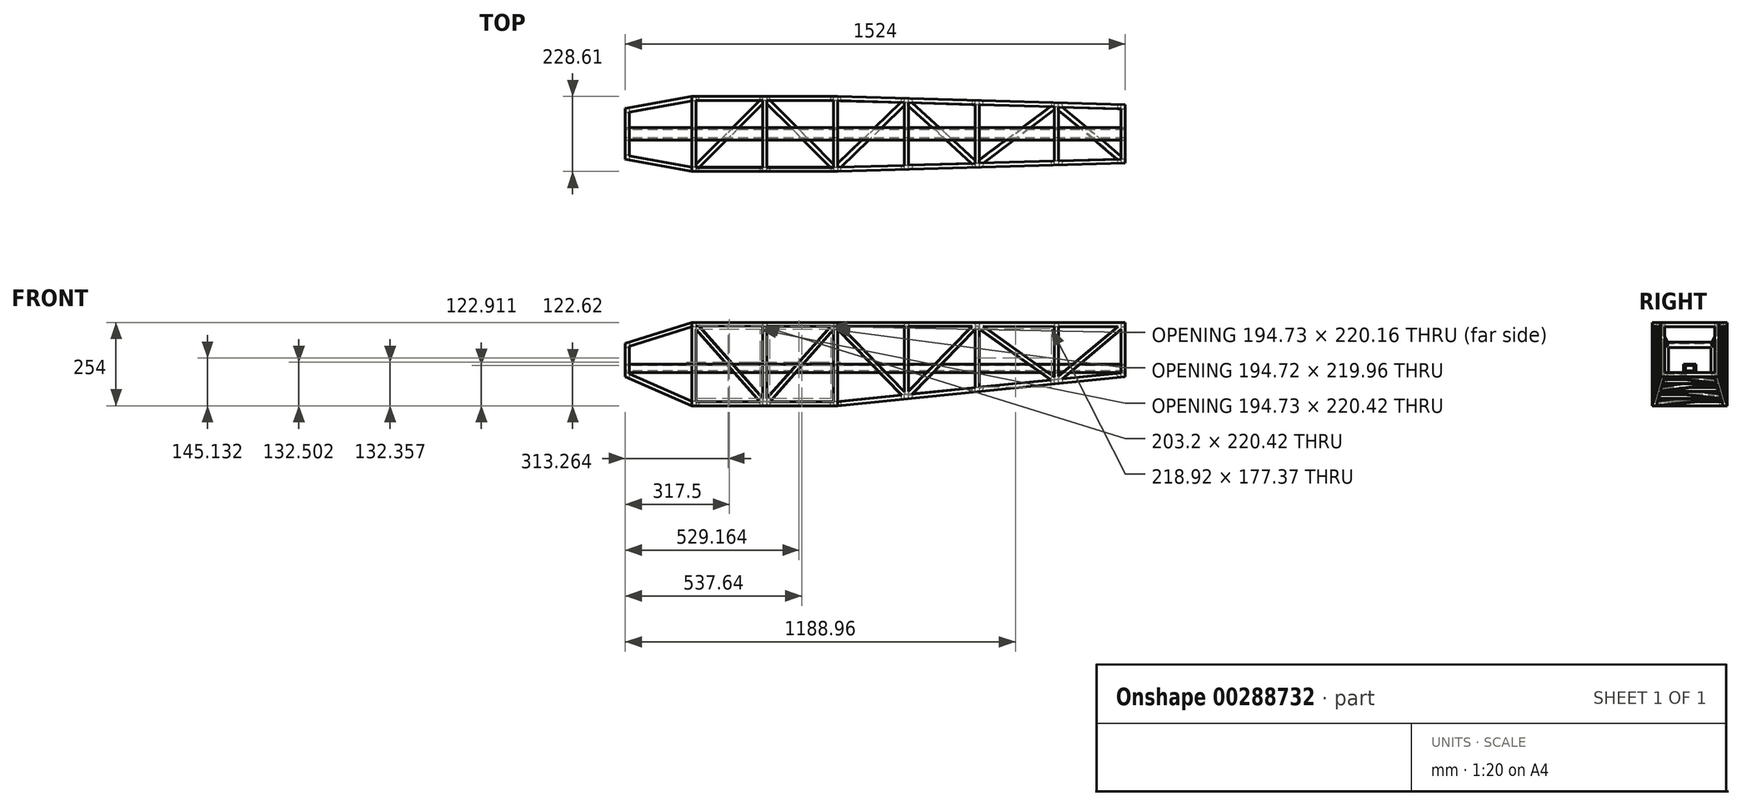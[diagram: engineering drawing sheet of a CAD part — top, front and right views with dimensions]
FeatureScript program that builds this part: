
annotation { "Feature Type Name" : "Feature", "Feature Type Description" : "" }
export const myFeature = defineFeature(function(context is Context, id is Id, definition is map)
    precondition{}
    {
        {
            var Q0;
            Q0=qCreatedBy(makeId("Top.planeOp"),FACE);
            var sketch = newSketch(context, id + "F0", { "sketchPlane" : qUnion([Q0])});
            skLineSegment(sketch, "E0.bottom", {"start": v(762, 177.8) * mm, "end": v(-762, 177.8) * mm});
            skLineSegment(sketch, "E0.top", {"start": v(762, -177.8) * mm, "end": v(-762, -177.8) * mm});
            skLineSegment(sketch, "E0.left", {"start": v(762, 177.8) * mm, "end": v(762, -177.8) * mm});
            skLineSegment(sketch, "E0.right", {"start": v(-762, 177.8) * mm, "end": v(-762, -177.8) * mm});
            skPoint(sketch, "E0.middle", {"position": v(0, 0) * mm});
            skSolve(sketch);
        }
        {
            var Q0;
            Q0=makeQuery(id+"F0.imprint","IMPRINT",FACE,{"disambiguationData":[TD([[makeQuery(id+"F0.imprint","IMPRINT",EDGE,{"derivedFrom":sQuery(id+"F0.wireOp",EDGE,"E0.bottom")}),1.0]])]});
            extrude(context, id + "F1", {"entities" : qUnion([Q0]), "endBound" : BoundingType.SYMMETRIC, "depth" : 254 * mm});
        }
        {
            var Q0;
            Q0=makeQuery(id+"F1.opExtrude","SWEPT_FACE",FACE,{"disambiguationData":[OSD([sQuery(id+"F0.wireOp",EDGE,"E0.left")])]});
            var sketch = newSketch(context, id + "F2", { "sketchPlane" : qUnion([Q0])});
            skLineSegment(sketch, "E1.0", {"start": v(-165.1, -114.3) * mm, "end": v(165.1, -114.3) * mm});
            skLineSegment(sketch, "E1.1", {"start": v(-165.1, 114.3) * mm, "end": v(-165.1, -114.3) * mm});
            skLineSegment(sketch, "E1.2", {"start": v(165.1, 114.3) * mm, "end": v(-165.1, 114.3) * mm});
            skLineSegment(sketch, "E1.3", {"start": v(165.1, -114.3) * mm, "end": v(165.1, 114.3) * mm});
            skSolve(sketch);
        }
        {
            var Q0;
            Q0=makeQuery(id+"F1.opExtrude","CAP_FACE",FACE,{"disambiguationData":[OSD([sQuery(id+"F0.wireOp",EDGE,"E0.bottom"),sQuery(id+"F0.wireOp",EDGE,"E0.top"),sQuery(id+"F0.wireOp",EDGE,"E0.left"),sQuery(id+"F0.wireOp",EDGE,"E0.right")])],"isStart":false});
            var sketch = newSketch(context, id + "F3", { "sketchPlane" : qUnion([Q0])});
            skLineSegment(sketch, "E2.0", {"start": v(-749.3, -165.1) * mm, "end": v(749.3, -165.1) * mm});
            skLineSegment(sketch, "E2.1", {"start": v(-749.3, 165.1) * mm, "end": v(-749.3, -165.1) * mm});
            skLineSegment(sketch, "E2.2", {"start": v(749.3, 165.1) * mm, "end": v(-749.3, 165.1) * mm});
            skLineSegment(sketch, "E2.3", {"start": v(749.3, -165.1) * mm, "end": v(749.3, 165.1) * mm});
            skSolve(sketch);
        }
        {
            var Q0;
            Q0=qCreatedBy(makeId("Front.planeOp"),FACE);
            var sketch = newSketch(context, id + "F4", { "sketchPlane" : qUnion([Q0])});
            skLineSegment(sketch, "E3.0", {"start": v(-762, 127) * mm, "end": v(-762, -127) * mm, "construction": true});
            skLineSegment(sketch, "E4.bottom", {"start": v(-558.8, -143.07) * mm, "end": v(-546.1, -143.07) * mm});
            skLineSegment(sketch, "E4.top", {"start": v(-558.8, 152.62) * mm, "end": v(-546.1, 152.62) * mm});
            skLineSegment(sketch, "E4.left", {"start": v(-558.8, -143.07) * mm, "end": v(-558.8, 152.62) * mm});
            skLineSegment(sketch, "E4.right", {"start": v(-546.1, -143.07) * mm, "end": v(-546.1, 152.62) * mm});
            skLineSegment(sketch, "E5.bottom", {"start": v(-342.9, -143.07) * mm, "end": v(-330.2, -143.07) * mm});
            skLineSegment(sketch, "E5.top", {"start": v(-342.9, 152.62) * mm, "end": v(-330.2, 152.62) * mm});
            skLineSegment(sketch, "E5.left", {"start": v(-342.9, -143.07) * mm, "end": v(-342.9, 152.62) * mm});
            skLineSegment(sketch, "E5.right", {"start": v(-330.2, -143.07) * mm, "end": v(-330.2, 152.62) * mm});
            skLineSegment(sketch, "E6.bottom", {"start": v(-127, -143.07) * mm, "end": v(-114.3, -143.07) * mm});
            skLineSegment(sketch, "E6.top", {"start": v(-127, 152.62) * mm, "end": v(-114.3, 152.62) * mm});
            skLineSegment(sketch, "E6.left", {"start": v(-127, -143.07) * mm, "end": v(-127, 152.62) * mm});
            skLineSegment(sketch, "E6.right", {"start": v(-114.3, -143.07) * mm, "end": v(-114.3, 152.62) * mm});
            skLineSegment(sketch, "E7.bottom", {"start": v(88.9, -143.07) * mm, "end": v(101.6, -143.07) * mm});
            skLineSegment(sketch, "E7.top", {"start": v(88.9, 152.62) * mm, "end": v(101.6, 152.62) * mm});
            skLineSegment(sketch, "E7.left", {"start": v(88.9, -143.07) * mm, "end": v(88.9, 152.62) * mm});
            skLineSegment(sketch, "E7.right", {"start": v(101.6, -143.07) * mm, "end": v(101.6, 152.62) * mm});
            skLineSegment(sketch, "E8", {"start": v(1356.57, 152.62) * mm, "end": v(-852.45, 152.62) * mm, "construction": true});
            skLineSegment(sketch, "E9", {"start": v(1396.25, -143.07) * mm, "end": v(-846.12, -143.07) * mm, "construction": true});
            skLineSegment(sketch, "E10.bottom", {"start": v(254, 152.62) * mm, "end": v(266.7, 152.62) * mm});
            skLineSegment(sketch, "E10.top", {"start": v(254, -143.07) * mm, "end": v(266.7, -143.07) * mm});
            skLineSegment(sketch, "E11.bottom", {"start": v(546.1, -143.07) * mm, "end": v(558.8, -143.07) * mm});
            skLineSegment(sketch, "E11.top", {"start": v(546.1, 152.62) * mm, "end": v(558.8, 152.62) * mm});
            skLineSegment(sketch, "E11.left", {"start": v(546.1, -143.07) * mm, "end": v(546.1, 152.62) * mm});
            skLineSegment(sketch, "E11.right", {"start": v(558.8, -143.07) * mm, "end": v(558.8, 152.62) * mm});
            skLineSegment(sketch, "E12.bottom", {"start": v(304.8, 152.62) * mm, "end": v(317.5, 152.62) * mm});
            skLineSegment(sketch, "E12.top", {"start": v(304.8, -143.07) * mm, "end": v(317.5, -143.07) * mm});
            skLineSegment(sketch, "E12.left", {"start": v(304.8, 152.62) * mm, "end": v(304.8, -143.07) * mm});
            skLineSegment(sketch, "E12.right", {"start": v(317.5, 152.62) * mm, "end": v(317.5, -143.07) * mm});
            skSolve(sketch);
        }
        {
            var Q0;
            Q0=qSketchRegion(id+"F4",true);
            extrude(context, id + "F5", {"entities" : qUnion([Q0]), "operationType" : NewBodyOperationType.ADD, "endBound" : BoundingType.SYMMETRIC, "depth" : 355.6 * mm});
        }
        {
            var Q0;
            Q0=qCreatedBy(makeId("Front.planeOp"),FACE);
            var sketch = newSketch(context, id + "F6", { "sketchPlane" : qUnion([Q0])});
            skLineSegment(sketch, "E13", {"start": v(-822.55, 43.96) * mm, "end": v(-558.8, 127) * mm});
            skLineSegment(sketch, "E14", {"start": v(-558.8, 127) * mm, "end": v(-1015.01, 307.35) * mm});
            skLineSegment(sketch, "E15", {"start": v(-1015.01, 307.35) * mm, "end": v(-822.55, 43.96) * mm});
            skLineSegment(sketch, "E16.0", {"start": v(-762, 127) * mm, "end": v(-762, -127) * mm, "construction": true});
            skLineSegment(sketch, "E17.0", {"start": v(762, 127) * mm, "end": v(762, -127) * mm, "construction": true});
            skLineSegment(sketch, "E18", {"start": v(-762, -38.1) * mm, "end": v(-558.8, -127) * mm});
            skLineSegment(sketch, "E19", {"start": v(-114.3, -127) * mm, "end": v(762, -38.1) * mm});
            skLineSegment(sketch, "E20", {"start": v(-762, -38.1) * mm, "end": v(-810.44, -38.1) * mm});
            skLineSegment(sketch, "E21", {"start": v(-810.44, -38.1) * mm, "end": v(-810.44, -218.05) * mm});
            skLineSegment(sketch, "E22", {"start": v(-810.44, -218.05) * mm, "end": v(819.71, -218.05) * mm});
            skLineSegment(sketch, "E23", {"start": v(819.71, -218.05) * mm, "end": v(819.71, -38.1) * mm});
            skLineSegment(sketch, "E24", {"start": v(819.71, -38.1) * mm, "end": v(762, -38.1) * mm});
            skLineSegment(sketch, "E25", {"start": v(-114.3, -127) * mm, "end": v(-558.8, -127) * mm});
            skSolve(sketch);
        }
        {
            var Q0;
            Q0=makeQuery(id+"F6.imprint","IMPRINT",FACE,{"disambiguationData":[TD([[makeQuery(id+"F6.imprint","IMPRINT",EDGE,{"derivedFrom":sQuery(id+"F6.wireOp",EDGE,"aae6dbfc-d4bc-4c02-a432-3037b792f5ca")}),1.0]])]});
            var Q1;
            Q1=makeQuery(id+"F6.imprint","IMPRINT",FACE,{"disambiguationData":[TD([[makeQuery(id+"F6.imprint","IMPRINT",EDGE,{"derivedFrom":sQuery(id+"F6.wireOp",EDGE,"E13")}),1.0]])]});
            var Q2;
            Q2=makeQuery(id+"F6.imprint","IMPRINT",FACE,{"disambiguationData":[TD([[makeQuery(id+"F6.imprint","IMPRINT",EDGE,{"derivedFrom":sQuery(id+"F6.wireOp",EDGE,"E18")}),-1.0]])]});
            extrude(context, id + "F7", {"entities" : qUnion([Q0, Q1, Q2]), "operationType" : NewBodyOperationType.REMOVE, "endBound" : BoundingType.SYMMETRIC, "oppositeDirection" : true, "depth" : 381 * mm});
        }
        {
            var Q0;
            Q0=qCreatedBy(makeId("Top.planeOp"),FACE);
            var sketch = newSketch(context, id + "F8", { "sketchPlane" : qUnion([Q0])});
            skLineSegment(sketch, "E26", {"start": v(-925.1, 0) * mm, "end": v(877.17, 0) * mm, "construction": true});
            skLineSegment(sketch, "E27", {"start": v(-885.68, 88.9) * mm, "end": v(840.74, 88.9) * mm, "construction": true});
            skLineSegment(sketch, "E28.0", {"start": v(-762, -177.8) * mm, "end": v(-762, 177.8) * mm, "construction": true});
            skLineSegment(sketch, "E29.0", {"start": v(762, 177.8) * mm, "end": v(762, -177.8) * mm, "construction": true});
            skLineSegment(sketch, "E30.0", {"start": v(-342.9, -368.3) * mm, "end": v(-342.9, -88.9) * mm, "construction": true});
            skLineSegment(sketch, "E31.0", {"start": v(101.6, -177.8) * mm, "end": v(101.6, 177.8) * mm, "construction": true});
            skLineSegment(sketch, "E32", {"start": v(762, 0) * mm, "end": v(762, 88.9) * mm});
            skLineSegment(sketch, "E33.0", {"start": v(-114.3, -177.8) * mm, "end": v(-114.3, 177.8) * mm, "construction": true});
            skLineSegment(sketch, "E34", {"start": v(-762, 77.57) * mm, "end": v(-762, 0) * mm});
            skLineSegment(sketch, "E35", {"start": v(-762, 0) * mm, "end": v(-762, 0) * mm});
            skLineSegment(sketch, "E36.MirrorCS", {"start": v(762, 0) * mm, "end": v(762, -88.9) * mm});
            skLineSegment(sketch, "E37.MirrorCS", {"start": v(-762, -77.57) * mm, "end": v(-762, 0) * mm});
            skLineSegment(sketch, "E38.MirrorCS", {"start": v(-885.68, -88.9) * mm, "end": v(840.74, -88.9) * mm, "construction": true});
            skLineSegment(sketch, "E39.MirrorCS", {"start": v(-762, 177.8) * mm, "end": v(-762, -177.8) * mm, "construction": true});
            skLineSegment(sketch, "E40.MirrorCS", {"start": v(762, -177.8) * mm, "end": v(762, 177.8) * mm, "construction": true});
            skLineSegment(sketch, "E41.MirrorCS", {"start": v(-342.9, 368.3) * mm, "end": v(-342.9, 88.9) * mm, "construction": true});
            skLineSegment(sketch, "E42.MirrorCS", {"start": v(-114.3, 177.8) * mm, "end": v(-114.3, -177.8) * mm, "construction": true});
            skLineSegment(sketch, "E43.MirrorCS", {"start": v(101.6, 177.8) * mm, "end": v(101.6, -177.8) * mm, "construction": true});
            skLineSegment(sketch, "E44.bottom", {"start": v(-858.41, 245.19) * mm, "end": v(858.29, 245.19) * mm});
            skLineSegment(sketch, "E44.top", {"start": v(-858.41, -226.45) * mm, "end": v(858.29, -226.45) * mm});
            skLineSegment(sketch, "E44.left", {"start": v(-858.41, 245.19) * mm, "end": v(-858.41, -226.45) * mm});
            skLineSegment(sketch, "E44.right", {"start": v(858.29, 245.19) * mm, "end": v(858.29, -226.45) * mm});
            skLineSegment(sketch, "E45", {"start": v(-342.9, 114.3) * mm, "end": v(-114.3, 114.3) * mm});
            skLineSegment(sketch, "E46.MirrorCS", {"start": v(-342.9, -114.3) * mm, "end": v(-114.3, -114.3) * mm});
            skLineSegment(sketch, "E47", {"start": v(-342.9, 114.3) * mm, "end": v(-558.8, 114.3) * mm});
            skLineSegment(sketch, "E48", {"start": v(-114.3, 114.3) * mm, "end": v(762, 88.9) * mm});
            skLineSegment(sketch, "E49", {"start": v(-342.9, -114.3) * mm, "end": v(-558.8, -114.3) * mm});
            skLineSegment(sketch, "E50", {"start": v(-114.3, -114.3) * mm, "end": v(762, -88.9) * mm});
            skLineSegment(sketch, "E51", {"start": v(-762, 77.57) * mm, "end": v(-558.8, 114.3) * mm});
            skLineSegment(sketch, "E52", {"start": v(-762, -77.57) * mm, "end": v(-558.8, -114.3) * mm});
            skSolve(sketch);
        }
        {
            var Q0;
            Q0=qSketchRegion(id+"F8",true);
            extrude(context, id + "F9", {"entities" : qUnion([Q0]), "operationType" : NewBodyOperationType.REMOVE, "endBound" : BoundingType.SYMMETRIC, "oppositeDirection" : true, "depth" : 381 * mm});
        }
        {
            var Q0;
            Q0=qCreatedBy(makeId("Top.planeOp"),FACE);
            var sketch = newSketch(context, id + "F10", { "sketchPlane" : qUnion([Q0])});
            skLineSegment(sketch, "E53.1", {"start": v(-749.3, -66.96) * mm, "end": v(-749.3, 66.96) * mm});
            skLineSegment(sketch, "E54.1", {"start": v(749.3, 76.56) * mm, "end": v(749.3, -76.56) * mm});
            skLineSegment(sketch, "E55.0", {"start": v(-127, 101.6) * mm, "end": v(-330.2, 101.6) * mm});
            skLineSegment(sketch, "E56.0", {"start": v(-330.2, -101.96) * mm, "end": v(-127, -101.96) * mm});
            skLineSegment(sketch, "E57.0", {"start": v(558.8, 82.08) * mm, "end": v(749.3, 76.56) * mm});
            skLineSegment(sketch, "E58.0", {"start": v(558.8, -82.08) * mm, "end": v(749.3, -76.56) * mm});
            skLineSegment(sketch, "E59.0", {"start": v(-749.3, -66.96) * mm, "end": v(-558.8, -101.4) * mm});
            skLineSegment(sketch, "E60", {"start": v(-342.9, -101.96) * mm, "end": v(-546.1, -101.96) * mm});
            skLineSegment(sketch, "E61", {"start": v(-546.1, 101.6) * mm, "end": v(-342.9, 101.6) * mm});
            skLineSegment(sketch, "E62.0.1", {"start": v(-546.1, -101.96) * mm, "end": v(-546.1, 101.6) * mm});
            skLineSegment(sketch, "E62.0.3", {"start": v(-558.8, 101.4) * mm, "end": v(-558.8, -101.4) * mm});
            skLineSegment(sketch, "E63.0.1", {"start": v(-342.9, 101.6) * mm, "end": v(-342.9, -101.96) * mm});
            skLineSegment(sketch, "E64.0.1", {"start": v(88.9, 95.71) * mm, "end": v(88.9, -95.7) * mm});
            skLineSegment(sketch, "E64.0.3", {"start": v(101.6, -95.34) * mm, "end": v(101.6, 95.34) * mm});
            skLineSegment(sketch, "E65.0.1", {"start": v(304.8, 89.45) * mm, "end": v(304.8, -89.45) * mm});
            skLineSegment(sketch, "E65.0.3", {"start": v(317.5, -89.08) * mm, "end": v(317.5, 89.08) * mm});
            skLineSegment(sketch, "E66.0.1", {"start": v(546.1, 82.45) * mm, "end": v(546.1, -82.45) * mm});
            skLineSegment(sketch, "E66.0.3", {"start": v(558.8, -82.08) * mm, "end": v(558.8, 82.08) * mm});
            skLineSegment(sketch, "E67.trimOffspring", {"start": v(304.8, -89.45) * mm, "end": v(101.6, -95.34) * mm});
            skLineSegment(sketch, "E68.trimOffspring", {"start": v(88.9, -95.7) * mm, "end": v(-114.3, -101.6) * mm});
            skLineSegment(sketch, "E69.trimOffspring", {"start": v(101.6, 95.34) * mm, "end": v(304.8, 89.45) * mm});
            skPoint(sketch, "E62.0.2.end.orphan", {"position": v(-558.8, 114.3) * mm});
            skPoint(sketch, "E62.0.2.start.orphan", {"position": v(-546.1, 114.3) * mm});
            skPoint(sketch, "E70.orphan", {"position": v(-558.8, -114.3) * mm});
            skPoint(sketch, "E71.orphan", {"position": v(-546.1, -114.3) * mm});
            skLineSegment(sketch, "E72", {"start": v(-749.3, 66.96) * mm, "end": v(-558.8, 101.4) * mm});
            skLineSegment(sketch, "E73", {"start": v(-114.3, -101.6) * mm, "end": v(-114.3, 101.6) * mm});
            skLineSegment(sketch, "E74", {"start": v(-330.2, 101.6) * mm, "end": v(-330.2, -101.96) * mm});
            skLineSegment(sketch, "E75", {"start": v(-127, 101.6) * mm, "end": v(-127, -101.96) * mm});
            skLineSegment(sketch, "E76", {"start": v(546.1, -82.45) * mm, "end": v(317.5, -89.08) * mm});
            skLineSegment(sketch, "E77", {"start": v(88.9, 95.71) * mm, "end": v(-114.3, 101.6) * mm});
            skLineSegment(sketch, "E78", {"start": v(546.1, 82.45) * mm, "end": v(317.5, 89.08) * mm});
            skSolve(sketch);
        }
        {
            var Q0;
            Q0=qSketchRegion(id+"F10",true);
            extrude(context, id + "F11", {"entities" : qUnion([Q0]), "operationType" : NewBodyOperationType.REMOVE, "endBound" : BoundingType.SYMMETRIC, "depth" : 381 * mm});
        }
        {
            var Q0;
            Q0=qCreatedBy(makeId("Front.planeOp"),FACE);
            var sketch = newSketch(context, id + "F12", { "sketchPlane" : qUnion([Q0])});
            skLineSegment(sketch, "E79.0", {"start": v(-749.3, 53.7) * mm, "end": v(-558.8, 113.69) * mm});
            skLineSegment(sketch, "E79.1", {"start": v(-749.3, -29.8) * mm, "end": v(-749.3, 53.7) * mm});
            skLineSegment(sketch, "E79.2", {"start": v(-749.3, -29.8) * mm, "end": v(-558.8, -113.14) * mm});
            skLineSegment(sketch, "E79.3", {"start": v(-342.9, -114.3) * mm, "end": v(-546.1, -114.3) * mm});
            skLineSegment(sketch, "E80.0", {"start": v(749.3, -26.62) * mm, "end": v(558.8, -45.95) * mm});
            skLineSegment(sketch, "E80.1", {"start": v(749.3, -26.62) * mm, "end": v(749.3, 114.3) * mm});
            skLineSegment(sketch, "E80.2", {"start": v(558.8, 114.3) * mm, "end": v(749.3, 114.3) * mm});
            skLineSegment(sketch, "E81", {"start": v(-127, -114.36) * mm, "end": v(-330.2, -114.3) * mm});
            skLineSegment(sketch, "E82.0.1", {"start": v(558.8, 114.3) * mm, "end": v(558.8, -45.95) * mm});
            skLineSegment(sketch, "E83.0.1", {"start": v(101.6, 114.89) * mm, "end": v(101.6, -92.46) * mm});
            skLineSegment(sketch, "E83.0.3", {"start": v(304.8, -71.84) * mm, "end": v(304.8, 114.63) * mm});
            skLineSegment(sketch, "E84.0.0", {"start": v(-330.2, 115.44) * mm, "end": v(-330.2, -114.3) * mm});
            skLineSegment(sketch, "E84.0.2", {"start": v(-127, -114.36) * mm, "end": v(-127, 115.18) * mm});
            skLineSegment(sketch, "E85.0.1", {"start": v(-546.1, 115.71) * mm, "end": v(-546.1, -114.3) * mm});
            skLineSegment(sketch, "E85.0.3", {"start": v(-342.9, -114.3) * mm, "end": v(-342.9, 115.45) * mm});
            skLineSegment(sketch, "E86.0.2", {"start": v(-558.8, -113.14) * mm, "end": v(-558.8, 113.69) * mm});
            skPoint(sketch, "E82.0.0.start.orphan", {"position": v(749.3, 127) * mm});
            skPoint(sketch, "E87.orphan", {"position": v(558.8, 127) * mm});
            skPoint(sketch, "E88.0.0.start.orphan", {"position": v(558.8, 126.99) * mm});
            skLineSegment(sketch, "E89.trimOffspring", {"start": v(304.8, 114.63) * mm, "end": v(101.6, 114.89) * mm});
            skPoint(sketch, "E83.0.0.start.orphan", {"position": v(304.8, 127) * mm});
            skLineSegment(sketch, "E90.trimOffspring", {"start": v(-127, 115.18) * mm, "end": v(-330.2, 115.44) * mm});
            skPoint(sketch, "E84.0.1.end.orphan", {"position": v(-127, -127) * mm});
            skPoint(sketch, "E91.orphan", {"position": v(-330.2, -127) * mm});
            skLineSegment(sketch, "E92.trimOffspring", {"start": v(-342.9, 115.45) * mm, "end": v(-546.1, 115.71) * mm});
            skPoint(sketch, "E84.0.3.end.orphan", {"position": v(-330.2, 127) * mm});
            skPoint(sketch, "E84.0.3.start.orphan", {"position": v(-127, 127) * mm});
            skPoint(sketch, "E85.0.2.end.orphan", {"position": v(-342.9, -127) * mm});
            skPoint(sketch, "E93.orphan", {"position": v(-546.1, -127) * mm});
            skPoint(sketch, "E94.orphan", {"position": v(-546.1, 127) * mm});
            skPoint(sketch, "E86.0.3.start.orphan", {"position": v(-558.8, 127) * mm});
            skPoint(sketch, "E95.orphan", {"position": v(101.6, 127) * mm});
            skLineSegment(sketch, "E96", {"start": v(546.1, -48.1) * mm, "end": v(456.3, -56.47) * mm});
            skPoint(sketch, "E82.0.2.end.orphan", {"position": v(749.3, -39.39) * mm});
            skPoint(sketch, "E97.orphan", {"position": v(-342.9, 127) * mm});
            skLineSegment(sketch, "E98.left", {"start": v(-680.76, 244.02) * mm, "end": v(-680.76, 242.67) * mm});
            skLineSegment(sketch, "E98.right", {"start": v(-640.08, 244.02) * mm, "end": v(-640.08, 242.67) * mm});
            skLineSegment(sketch, "E99.bottom", {"start": v(851.63, 270.75) * mm, "end": v(-718.73, 270.75) * mm});
            skLineSegment(sketch, "E99.top", {"start": v(851.63, 127) * mm, "end": v(-718.73, 127) * mm});
            skLineSegment(sketch, "E99.left", {"start": v(851.63, 270.75) * mm, "end": v(851.63, 127) * mm});
            skLineSegment(sketch, "E99.right", {"start": v(-718.73, 270.75) * mm, "end": v(-718.73, 127) * mm});
            skLineSegment(sketch, "E100", {"start": v(-114.3, -114.36) * mm, "end": v(88.9, -93.75) * mm});
            skLineSegment(sketch, "E101", {"start": v(546.1, 114.3) * mm, "end": v(317.5, 114.61) * mm});
            skLineSegment(sketch, "E102", {"start": v(88.9, 114.9) * mm, "end": v(-114.3, 115.18) * mm});
            skLineSegment(sketch, "E103", {"start": v(-114.3, 115.18) * mm, "end": v(-114.3, -114.36) * mm});
            skLineSegment(sketch, "E104", {"start": v(88.9, 114.9) * mm, "end": v(88.9, -93.75) * mm});
            skLineSegment(sketch, "E105", {"start": v(317.5, 114.61) * mm, "end": v(317.5, -70.55) * mm});
            skLineSegment(sketch, "E106", {"start": v(546.1, 114.3) * mm, "end": v(546.1, -48.1) * mm});
            skLineSegment(sketch, "E107.trimOffspring", {"start": v(317.5, -70.55) * mm, "end": v(456.3, -56.47) * mm});
            skLineSegment(sketch, "E108.trimOffspring", {"start": v(101.6, -92.46) * mm, "end": v(304.8, -71.84) * mm});
            skSolve(sketch);
        }
        {
            var Q0;
            Q0=qSketchRegion(id+"F12",true);
            extrude(context, id + "F13", {"entities" : qUnion([Q0]), "operationType" : NewBodyOperationType.REMOVE, "endBound" : BoundingType.SYMMETRIC, "oppositeDirection" : true, "depth" : 381 * mm});
        }
        {
            var Q0;
            {var subQ4=sQuery(id+"F4.wireOp",EDGE,"E4.top");var subQ11=sQuery(id+"F4.wireOp",EDGE,"E4.left");Q0=makeQuery(id+"F13.boolean.opBoolean","MERGE",FACE,{"derivedFrom":[makeQuery(id+"F11.boolean.opBoolean","MERGE",FACE,{"derivedFrom":[makeQuery(id+"F5.boolean.opBoolean","SPLIT",FACE,{"disambiguationData":[TD([makeQuery(id+"F5.opExtrude","SWEPT_FACE",FACE,{"disambiguationData":[OSD([subQ4])]})])],"derivedFrom":makeQuery(id+"F5.opExtrude","SWEPT_FACE",FACE,{"disambiguationData":[OSD([subQ11])]})}),makeQuery(id+"F11.opExtrude","SWEPT_FACE",FACE,{"disambiguationData":[OSD([sQuery(id+"F10.wireOp",EDGE,"76c89935-962c-43c5-8293-adbbc792d1c5.0")])]})]}),makeQuery(id+"F13.opExtrude","SWEPT_FACE",FACE,{"disambiguationData":[OSD([sQuery(id+"F12.wireOp",EDGE,"9ef2c277-a94d-4be6-9fd4-f6ea86bf56da.0.3")])]})]});}
            var sketch = newSketch(context, id + "F14", { "sketchPlane" : qUnion([Q0])});
            skLineSegment(sketch, "E109.bottom", {"start": v(-101.4, 113.69) * mm, "end": v(101.4, 113.69) * mm});
            skLineSegment(sketch, "E109.top", {"start": v(-101.4, -113.14) * mm, "end": v(101.4, -113.14) * mm});
            skLineSegment(sketch, "E109.left", {"start": v(-101.4, 113.69) * mm, "end": v(-101.4, -113.14) * mm});
            skLineSegment(sketch, "E109.right", {"start": v(101.4, 113.69) * mm, "end": v(101.4, -113.14) * mm});
            skSolve(sketch);
        }
        {
            var Q0;
            Q0=qSketchRegion(id+"F14",true);
            extrude(context, id + "F15", {"entities" : qUnion([Q0]), "operationType" : NewBodyOperationType.REMOVE, "oppositeDirection" : true, "depth" : 25.4 * mm});
        }
        {
            var Q0;
            {var subQ1=sQuery(id+"F4.wireOp",EDGE,"E5.left");var subQ2=sQuery(id+"F4.wireOp",EDGE,"E5.top");Q0=makeQuery(id+"F13.boolean.opBoolean","MERGE",FACE,{"derivedFrom":[makeQuery(id+"F11.boolean.opBoolean","MERGE",FACE,{"derivedFrom":[makeQuery(id+"F5.boolean.opBoolean","SPLIT",FACE,{"disambiguationData":[TD([makeQuery(id+"F5.opExtrude","SWEPT_FACE",FACE,{"disambiguationData":[OSD([subQ2])]})])],"derivedFrom":makeQuery(id+"F5.opExtrude","SWEPT_FACE",FACE,{"disambiguationData":[OSD([subQ1])]})}),makeQuery(id+"F11.opExtrude","SWEPT_FACE",FACE,{"disambiguationData":[OSD([sQuery(id+"F10.wireOp",EDGE,"7b3102ac-ed15-4f5d-bc17-57cfcd7eebf1.0")])]})]}),makeQuery(id+"F13.opExtrude","SWEPT_FACE",FACE,{"disambiguationData":[OSD([sQuery(id+"F12.wireOp",EDGE,"8vpACN4d-Oada-hr1t-Xb63-NezVnV2j5PEM")])]})]});}
            var sketch = newSketch(context, id + "F16", { "sketchPlane" : qUnion([Q0])});
            skLineSegment(sketch, "E110.bottom", {"start": v(-101.6, 115.45) * mm, "end": v(101.96, 115.45) * mm});
            skLineSegment(sketch, "E110.top", {"start": v(-101.6, -114.3) * mm, "end": v(101.96, -114.3) * mm});
            skLineSegment(sketch, "E110.left", {"start": v(-101.6, 115.45) * mm, "end": v(-101.6, -114.3) * mm});
            skLineSegment(sketch, "E110.right", {"start": v(101.96, 115.45) * mm, "end": v(101.96, -114.3) * mm});
            skSolve(sketch);
        }
        {
            var Q0;
            Q0=qSketchRegion(id+"F16",true);
            extrude(context, id + "F17", {"entities" : qUnion([Q0]), "operationType" : NewBodyOperationType.REMOVE, "oppositeDirection" : true, "depth" : 25.4 * mm});
        }
        {
            var Q0;
            {var subQ8=sQuery(id+"F4.wireOp",EDGE,"E6.top");var subQ16=sQuery(id+"F4.wireOp",EDGE,"E6.left");Q0=makeQuery(id+"F13.boolean.opBoolean","MERGE",FACE,{"derivedFrom":[makeQuery(id+"F11.boolean.opBoolean","MERGE",FACE,{"derivedFrom":[makeQuery(id+"F5.boolean.opBoolean","SPLIT",FACE,{"disambiguationData":[TD([makeQuery(id+"F5.opExtrude","SWEPT_FACE",FACE,{"disambiguationData":[OSD([subQ8])]})])],"derivedFrom":makeQuery(id+"F5.opExtrude","SWEPT_FACE",FACE,{"disambiguationData":[OSD([subQ16])]})}),makeQuery(id+"F11.opExtrude","SWEPT_FACE",FACE,{"disambiguationData":[OSD([sQuery(id+"F10.wireOp",EDGE,"b35c1112-db7b-4928-a18e-9a17467dcdab.0")])]})]}),makeQuery(id+"F13.opExtrude","SWEPT_FACE",FACE,{"disambiguationData":[OSD([sQuery(id+"F12.wireOp",EDGE,"fa40cc79-636a-4cbc-a25d-f27d8fe22ac2.0.3")])]})]});}
            var sketch = newSketch(context, id + "F18", { "sketchPlane" : qUnion([Q0])});
            skLineSegment(sketch, "E111.bottom", {"start": v(-101.6, 115.18) * mm, "end": v(101.96, 115.18) * mm});
            skLineSegment(sketch, "E111.top", {"start": v(-101.6, -114.36) * mm, "end": v(101.96, -114.36) * mm});
            skLineSegment(sketch, "E111.left", {"start": v(-101.6, 115.18) * mm, "end": v(-101.6, -114.36) * mm});
            skLineSegment(sketch, "E111.right", {"start": v(101.96, 115.18) * mm, "end": v(101.96, -114.36) * mm});
            skSolve(sketch);
        }
        {
            var Q0;
            Q0=qSketchRegion(id+"F18",true);
            extrude(context, id + "F19", {"entities" : qUnion([Q0]), "operationType" : NewBodyOperationType.REMOVE, "oppositeDirection" : true, "depth" : 25.4 * mm});
        }
        {
            var Q0;
            {var subQ0=sQuery(id+"F4.wireOp",EDGE,"E7.bottom");var subQ36=sQuery(id+"F4.wireOp",EDGE,"E7.left");var subQ37=sQuery(id+"F4.wireOp",EDGE,"E7.top");var subQ60=makeQuery(id+"F5.opExtrude","SWEPT_FACE",FACE,{"disambiguationData":[OSD([subQ36])]});Q0=makeQuery(id+"F13.boolean.opBoolean","MERGE",FACE,{"derivedFrom":[makeQuery(id+"F11.boolean.opBoolean","MERGE",FACE,{"derivedFrom":[makeQuery(id+"F5.boolean.opBoolean","SPLIT",FACE,{"disambiguationData":[TD([makeQuery(id+"F5.opExtrude","SWEPT_FACE",FACE,{"disambiguationData":[OSD([subQ37])]})])],"derivedFrom":subQ60}),makeQuery(id+"F5.boolean.opBoolean","SPLIT",FACE,{"disambiguationData":[TD([makeQuery(id+"F5.opExtrude","SWEPT_FACE",FACE,{"disambiguationData":[OSD([subQ0])]})])],"derivedFrom":subQ60}),makeQuery(id+"F11.opExtrude","SWEPT_FACE",FACE,{"disambiguationData":[OSD([sQuery(id+"F10.wireOp",EDGE,"7310f20e-b108-4276-8773-8cf4f74fe12c.0")])]})]}),makeQuery(id+"F13.opExtrude","SWEPT_FACE",FACE,{"disambiguationData":[OSD([sQuery(id+"F12.wireOp",EDGE,"FrRoJ9V7-tiAn-pTb4-UzEj-WxOpO9FH2ecp")])]})]});}
            var sketch = newSketch(context, id + "F20", { "sketchPlane" : qUnion([Q0])});
            skLineSegment(sketch, "E112.bottom", {"start": v(-95.71, 114.9) * mm, "end": v(95.7, 114.9) * mm});
            skLineSegment(sketch, "E112.top", {"start": v(-95.71, -93.75) * mm, "end": v(95.7, -93.75) * mm});
            skLineSegment(sketch, "E112.left", {"start": v(-95.71, 114.9) * mm, "end": v(-95.71, -93.75) * mm});
            skLineSegment(sketch, "E112.right", {"start": v(95.7, 114.9) * mm, "end": v(95.7, -93.75) * mm});
            skSolve(sketch);
        }
        {
            var Q0;
            Q0=qSketchRegion(id+"F20",true);
            extrude(context, id + "F21", {"entities" : qUnion([Q0]), "operationType" : NewBodyOperationType.REMOVE, "oppositeDirection" : true, "depth" : 25.4 * mm});
        }
        {
            var Q0;
            {var subQ35=sQuery(id+"F4.wireOp",EDGE,"E12.left");var subQ37=sQuery(id+"F4.wireOp",EDGE,"E12.bottom");Q0=makeQuery(id+"F13.boolean.opBoolean","MERGE",FACE,{"derivedFrom":[makeQuery(id+"F11.boolean.opBoolean","MERGE",FACE,{"derivedFrom":[makeQuery(id+"F5.boolean.opBoolean","SPLIT",FACE,{"disambiguationData":[TD([makeQuery(id+"F5.opExtrude","SWEPT_FACE",FACE,{"disambiguationData":[OSD([subQ37])]})])],"derivedFrom":makeQuery(id+"F5.opExtrude","SWEPT_FACE",FACE,{"disambiguationData":[OSD([subQ35])]})}),makeQuery(id+"F11.opExtrude","SWEPT_FACE",FACE,{"disambiguationData":[OSD([sQuery(id+"F10.wireOp",EDGE,"b7ba8543-acbf-43cf-88d8-2159336d2e7e.0")])]})]}),makeQuery(id+"F13.opExtrude","SWEPT_FACE",FACE,{"disambiguationData":[OSD([sQuery(id+"F12.wireOp",EDGE,"MzW9eNza-KUkf-pAGu-OPrh-YCygVrhiN9A4")])]})]});}
            var sketch = newSketch(context, id + "F22", { "sketchPlane" : qUnion([Q0])});
            skLineSegment(sketch, "E113.bottom", {"start": v(-89.45, 114.63) * mm, "end": v(89.45, 114.63) * mm});
            skLineSegment(sketch, "E113.top", {"start": v(-89.45, -71.84) * mm, "end": v(89.45, -71.84) * mm});
            skLineSegment(sketch, "E113.left", {"start": v(-89.45, 114.63) * mm, "end": v(-89.45, -71.84) * mm});
            skLineSegment(sketch, "E113.right", {"start": v(89.45, 114.63) * mm, "end": v(89.45, -71.84) * mm});
            skSolve(sketch);
        }
        {
            var Q0;
            Q0=qSketchRegion(id+"F22",true);
            extrude(context, id + "F23", {"entities" : qUnion([Q0]), "operationType" : NewBodyOperationType.REMOVE, "oppositeDirection" : true, "depth" : 15.24 * mm});
        }
        {
            var Q0;
            {var subQ18=sQuery(id+"F4.wireOp",EDGE,"E11.left");var subQ19=sQuery(id+"F4.wireOp",EDGE,"E11.top");Q0=makeQuery(id+"F13.boolean.opBoolean","MERGE",FACE,{"derivedFrom":[makeQuery(id+"F11.boolean.opBoolean","MERGE",FACE,{"derivedFrom":[makeQuery(id+"F5.boolean.opBoolean","SPLIT",FACE,{"disambiguationData":[TD([makeQuery(id+"F5.opExtrude","SWEPT_FACE",FACE,{"disambiguationData":[OSD([subQ19])]})])],"derivedFrom":makeQuery(id+"F5.opExtrude","SWEPT_FACE",FACE,{"disambiguationData":[OSD([subQ18])]})}),makeQuery(id+"F11.opExtrude","SWEPT_FACE",FACE,{"disambiguationData":[OSD([sQuery(id+"F10.wireOp",EDGE,"94f42aec-5a63-4bb3-a17e-c23af455982a.0")])]})]}),makeQuery(id+"F13.opExtrude","SWEPT_FACE",FACE,{"disambiguationData":[OSD([sQuery(id+"F12.wireOp",EDGE,"4bo9Z2lR-88Dg-C45D-lGNA-9ZzvTnCFj7b6")])]})]});}
            var sketch = newSketch(context, id + "F24", { "sketchPlane" : qUnion([Q0])});
            skLineSegment(sketch, "E114.bottom", {"start": v(-82.45, 114.3) * mm, "end": v(82.45, 114.3) * mm});
            skLineSegment(sketch, "E114.top", {"start": v(-82.45, -48.1) * mm, "end": v(82.45, -48.1) * mm});
            skLineSegment(sketch, "E114.left", {"start": v(82.45, 114.3) * mm, "end": v(82.45, -48.1) * mm});
            skLineSegment(sketch, "E114.right", {"start": v(-82.45, 114.3) * mm, "end": v(-82.45, -48.1) * mm});
            skSolve(sketch);
        }
        {
            var Q0;
            Q0=qSketchRegion(id+"F24",true);
            extrude(context, id + "F25", {"entities" : qUnion([Q0]), "operationType" : NewBodyOperationType.REMOVE, "oppositeDirection" : true, "depth" : 13.97 * mm});
        }
        {
            var Q0;
            Q0=makeQuery(id+"F1.opExtrude","SWEPT_FACE",FACE,{"disambiguationData":[OSD([sQuery(id+"F0.wireOp",EDGE,"E0.left")])]});
            var sketch = newSketch(context, id + "F26", { "sketchPlane" : qUnion([Q0])});
            skLineSegment(sketch, "E115.bottom", {"start": v(-76.2, 114.3) * mm, "end": v(76.2, 114.3) * mm});
            skLineSegment(sketch, "E115.top", {"start": v(-76.2, -25.4) * mm, "end": v(76.2, -25.4) * mm});
            skLineSegment(sketch, "E115.left", {"start": v(-76.2, 114.3) * mm, "end": v(-76.2, -25.4) * mm});
            skLineSegment(sketch, "E115.right", {"start": v(76.2, 114.3) * mm, "end": v(76.2, -25.4) * mm});
            skSolve(sketch);
        }
        {
            var Q0;
            Q0=makeQuery(id+"F26.imprint","IMPRINT",FACE,{"disambiguationData":[TD([[makeQuery(id+"F26.imprint","IMPRINT",EDGE,{"derivedFrom":sQuery(id+"F26.wireOp",EDGE,"E115.bottom")}),-1.0]])]});
            extrude(context, id + "F27", {"entities" : qUnion([Q0]), "operationType" : NewBodyOperationType.REMOVE, "oppositeDirection" : true, "depth" : 12.7 * mm});
        }
        {
            var Q0;
            Q0=makeQuery(id+"F9.boolean.opBoolean","COPY",FACE,{"derivedFrom":makeQuery(id+"F9.opExtrude","SWEPT_FACE",FACE,{"disambiguationData":[OSD([sQuery(id+"F8.wireOp",EDGE,"E50")])]})});
            var sketch = newSketch(context, id + "F28", { "sketchPlane" : qUnion([Q0])});
            skLineSegment(sketch, "E116", {"start": v(746.4, 114.3) * mm, "end": v(555.82, -45.95) * mm, "construction": true});
            skLineSegment(sketch, "E117", {"start": v(543.11, -48.1) * mm, "end": v(314.42, 114.61) * mm, "construction": true});
            skLineSegment(sketch, "E118", {"start": v(301.71, 114.63) * mm, "end": v(98.43, -92.46) * mm, "construction": true});
            skLineSegment(sketch, "E119", {"start": v(85.72, -93.75) * mm, "end": v(-117.56, 115.18) * mm, "construction": true});
            skLineSegment(sketch, "E120", {"start": v(746.4, 106) * mm, "end": v(567.04, -44.81) * mm});
            skLineSegment(sketch, "E121", {"start": v(533.43, -49) * mm, "end": v(314.42, 106.82) * mm});
            skLineSegment(sketch, "E122", {"start": v(108.3, -91.45) * mm, "end": v(301.71, 105.56) * mm});
            skLineSegment(sketch, "E123", {"start": v(-117.56, 106.07) * mm, "end": v(77.66, -94.56) * mm});
            skLineSegment(sketch, "E124.MirrorCS", {"start": v(736.53, 114.3) * mm, "end": v(558.87, -35.1) * mm});
            skLineSegment(sketch, "E125.MirrorCS", {"start": v(540.8, -38.66) * mm, "end": v(325.4, 114.6) * mm});
            skLineSegment(sketch, "E126.MirrorCS", {"start": v(99.25, -82.56) * mm, "end": v(292.65, 114.46) * mm});
            skLineSegment(sketch, "E127.MirrorCS", {"start": v(-108.46, 114.93) * mm, "end": v(85.72, -84.64) * mm});
            skPoint(sketch, "E128", {"position": v(736.53, 114.3) * mm});
            skPoint(sketch, "E129", {"position": v(325.4, 114.6) * mm});
            skPoint(sketch, "E130", {"position": v(85.72, -84.64) * mm});
            skPoint(sketch, "E131.orphan", {"position": v(738.23, 115.72) * mm});
            skLineSegment(sketch, "E132", {"start": v(558.87, -35.1) * mm, "end": v(555.82, -37.65) * mm});
            skLineSegment(sketch, "E133", {"start": v(540.8, -38.66) * mm, "end": v(543.11, -40.3) * mm});
            skPoint(sketch, "E134.orphan", {"position": v(321.78, 117.17) * mm});
            skLineSegment(sketch, "E135", {"start": v(292.65, 114.46) * mm, "end": v(292.83, 114.64) * mm});
            skLineSegment(sketch, "E136", {"start": v(99.25, -82.56) * mm, "end": v(98.43, -83.4) * mm});
            skPoint(sketch, "E137.orphan", {"position": v(86.76, -85.7) * mm});
            skLineSegment(sketch, "E138", {"start": v(-108.46, 114.93) * mm, "end": v(-108.7, 115.17) * mm});
            skLineSegment(sketch, "E139", {"start": v(-108.7, 115.17) * mm, "end": v(-117.56, 115.18) * mm});
            skLineSegment(sketch, "E140", {"start": v(-117.56, 115.18) * mm, "end": v(-117.56, 106.07) * mm});
            skLineSegment(sketch, "E141", {"start": v(85.72, -84.64) * mm, "end": v(85.72, -93.75) * mm});
            skLineSegment(sketch, "E142", {"start": v(77.66, -94.56) * mm, "end": v(85.72, -93.75) * mm});
            skLineSegment(sketch, "E143", {"start": v(98.43, -83.4) * mm, "end": v(98.43, -92.46) * mm});
            skLineSegment(sketch, "E144", {"start": v(108.3, -91.45) * mm, "end": v(98.43, -92.46) * mm});
            skLineSegment(sketch, "E145", {"start": v(301.71, 105.56) * mm, "end": v(301.71, 114.63) * mm});
            skLineSegment(sketch, "E146", {"start": v(292.83, 114.64) * mm, "end": v(301.71, 114.63) * mm});
            skLineSegment(sketch, "E147", {"start": v(325.4, 114.6) * mm, "end": v(314.42, 114.61) * mm});
            skLineSegment(sketch, "E148", {"start": v(314.42, 106.82) * mm, "end": v(314.42, 114.61) * mm});
            skLineSegment(sketch, "E149", {"start": v(533.43, -49) * mm, "end": v(543.11, -48.1) * mm});
            skLineSegment(sketch, "E150", {"start": v(543.11, -40.3) * mm, "end": v(543.11, -48.1) * mm});
            skLineSegment(sketch, "E151", {"start": v(555.82, -37.65) * mm, "end": v(555.82, -45.95) * mm});
            skLineSegment(sketch, "E152", {"start": v(567.04, -44.81) * mm, "end": v(555.82, -45.95) * mm});
            skLineSegment(sketch, "E153", {"start": v(746.4, 106) * mm, "end": v(746.4, 114.3) * mm});
            skLineSegment(sketch, "E154", {"start": v(736.53, 114.3) * mm, "end": v(746.4, 114.3) * mm});
            skSolve(sketch);
        }
        {
            var Q0;
            Q0=makeQuery(id+"F9.boolean.opBoolean","COPY",FACE,{"derivedFrom":makeQuery(id+"F9.opExtrude","SWEPT_FACE",FACE,{"disambiguationData":[OSD([sQuery(id+"F8.wireOp",EDGE,"E46.MirrorCS")])]})});
            var sketch = newSketch(context, id + "F29", { "sketchPlane" : qUnion([Q0])});
            skLineSegment(sketch, "E155", {"start": v(-127, 115.18) * mm, "end": v(-330.2, -114.3) * mm, "construction": true});
            skLineSegment(sketch, "E156", {"start": v(-135.47, 115.2) * mm, "end": v(-330.2, -104.72) * mm});
            skLineSegment(sketch, "E157", {"start": v(-135.47, 115.2) * mm, "end": v(-127, 115.18) * mm});
            skLineSegment(sketch, "E158", {"start": v(-127, 115.18) * mm, "end": v(-127, 105.6) * mm});
            skLineSegment(sketch, "E159", {"start": v(-127, 105.6) * mm, "end": v(-321.72, -114.3) * mm});
            skLineSegment(sketch, "E160", {"start": v(-321.72, -114.3) * mm, "end": v(-330.2, -114.3) * mm});
            skLineSegment(sketch, "E161", {"start": v(-330.2, -104.72) * mm, "end": v(-330.2, -114.3) * mm});
            skLineSegment(sketch, "E162", {"start": v(-546.1, 115.71) * mm, "end": v(-342.9, -114.3) * mm, "construction": true});
            skLineSegment(sketch, "E163", {"start": v(-342.9, -114.3) * mm, "end": v(-342.9, -104.7) * mm});
            skLineSegment(sketch, "E164", {"start": v(-342.9, -104.7) * mm, "end": v(-537.4, 115.45) * mm});
            skLineSegment(sketch, "E165", {"start": v(-537.4, 115.45) * mm, "end": v(-546.1, 115.71) * mm});
            skLineSegment(sketch, "E166", {"start": v(-546.1, 106.12) * mm, "end": v(-351.37, -114.3) * mm});
            skLineSegment(sketch, "E167", {"start": v(-351.37, -114.3) * mm, "end": v(-342.9, -114.3) * mm});
            skSolve(sketch);
        }
        {
            var Q0;
            Q0=makeQuery(id+"F9.boolean.opBoolean","COPY",FACE,{"derivedFrom":makeQuery(id+"F9.opExtrude","SWEPT_FACE",FACE,{"disambiguationData":[OSD([sQuery(id+"F8.wireOp",EDGE,"E48")])]})});
            var sketch = newSketch(context, id + "F30", { "sketchPlane" : qUnion([Q0])});
            skLineSegment(sketch, "E168", {"start": v(-746.4, 114.3) * mm, "end": v(-555.82, -45.95) * mm, "construction": true});
            skLineSegment(sketch, "E169", {"start": v(-555.82, -45.95) * mm, "end": v(-567.04, -44.81) * mm});
            skLineSegment(sketch, "E170", {"start": v(-567.04, -44.81) * mm, "end": v(-746.4, 106) * mm});
            skLineSegment(sketch, "E171", {"start": v(-746.4, 106) * mm, "end": v(-746.4, 114.3) * mm});
            skLineSegment(sketch, "E172", {"start": v(-746.4, 114.3) * mm, "end": v(-736.53, 114.3) * mm});
            skLineSegment(sketch, "E173", {"start": v(-736.53, 114.3) * mm, "end": v(-555.82, -37.65) * mm});
            skLineSegment(sketch, "E174", {"start": v(-555.82, -37.65) * mm, "end": v(-555.82, -45.95) * mm});
            skLineSegment(sketch, "E175", {"start": v(-543.11, -48.1) * mm, "end": v(-314.42, 114.61) * mm, "construction": true});
            skLineSegment(sketch, "E176", {"start": v(-314.42, 114.61) * mm, "end": v(-325.4, 114.6) * mm});
            skLineSegment(sketch, "E177", {"start": v(-325.4, 114.6) * mm, "end": v(-543.11, -40.3) * mm});
            skLineSegment(sketch, "E178", {"start": v(-543.11, -40.3) * mm, "end": v(-543.11, -48.1) * mm});
            skLineSegment(sketch, "E179", {"start": v(-543.11, -48.1) * mm, "end": v(-533.43, -49) * mm});
            skLineSegment(sketch, "E180", {"start": v(-533.43, -49) * mm, "end": v(-314.42, 106.82) * mm});
            skLineSegment(sketch, "E181", {"start": v(-314.42, 106.82) * mm, "end": v(-314.42, 114.61) * mm});
            skLineSegment(sketch, "E182", {"start": v(-325.4, 114.6) * mm, "end": v(-314.42, 114.61) * mm});
            skLineSegment(sketch, "E183", {"start": v(-301.71, 114.63) * mm, "end": v(-98.43, -92.46) * mm, "construction": true});
            skLineSegment(sketch, "E184", {"start": v(117.56, 115.18) * mm, "end": v(-85.72, -93.75) * mm, "construction": true});
            skLineSegment(sketch, "E185", {"start": v(-301.71, 114.63) * mm, "end": v(-292.83, 114.64) * mm});
            skLineSegment(sketch, "E186", {"start": v(-292.83, 114.64) * mm, "end": v(-98.43, -83.4) * mm});
            skLineSegment(sketch, "E187", {"start": v(-98.43, -83.4) * mm, "end": v(-98.43, -92.46) * mm});
            skLineSegment(sketch, "E188", {"start": v(-108.3, -91.45) * mm, "end": v(-98.43, -92.46) * mm});
            skLineSegment(sketch, "E189", {"start": v(-108.3, -91.45) * mm, "end": v(-301.71, 105.56) * mm});
            skLineSegment(sketch, "E190", {"start": v(-301.71, 105.56) * mm, "end": v(-301.71, 114.63) * mm});
            skLineSegment(sketch, "E191", {"start": v(-85.72, -93.75) * mm, "end": v(-85.72, -84.64) * mm});
            skLineSegment(sketch, "E192", {"start": v(-85.72, -84.64) * mm, "end": v(108.7, 115.17) * mm});
            skLineSegment(sketch, "E193", {"start": v(108.7, 115.17) * mm, "end": v(117.56, 115.18) * mm});
            skLineSegment(sketch, "E194", {"start": v(117.56, 115.18) * mm, "end": v(117.58, 106.09) * mm});
            skLineSegment(sketch, "E195", {"start": v(117.58, 106.09) * mm, "end": v(-77.66, -94.56) * mm});
            skLineSegment(sketch, "E196", {"start": v(-77.66, -94.56) * mm, "end": v(-85.72, -93.75) * mm});
            skSolve(sketch);
        }
        {
            var Q0;
            Q0=qSketchRegion(id+"F28",true);
            extrude(context, id + "F31", {"entities" : qUnion([Q0]), "oppositeDirection" : true, "depth" : 12.7 * mm});
        }
        {
            var Q0;
            Q0=makeQuery(id+"F9.boolean.opBoolean","COPY",FACE,{"derivedFrom":makeQuery(id+"F9.opExtrude","SWEPT_FACE",FACE,{"disambiguationData":[OSD([sQuery(id+"F8.wireOp",EDGE,"E45"),sQuery(id+"F8.wireOp",EDGE,"E47")])]})});
            var sketch = newSketch(context, id + "F32", { "sketchPlane" : qUnion([Q0])});
            skLineSegment(sketch, "E197.0", {"start": v(135.47, 115.2) * mm, "end": v(330.2, -104.72) * mm});
            skLineSegment(sketch, "E198.0", {"start": v(127, 105.6) * mm, "end": v(321.72, -114.3) * mm});
            skLineSegment(sketch, "E199.0", {"start": v(342.9, -104.7) * mm, "end": v(537.4, 115.45) * mm});
            skLineSegment(sketch, "E200.0", {"start": v(546.1, 106.12) * mm, "end": v(351.37, -114.3) * mm});
            skLineSegment(sketch, "E201.0", {"start": v(537.4, 115.45) * mm, "end": v(546.1, 115.71) * mm});
            skLineSegment(sketch, "E202", {"start": v(546.1, 115.71) * mm, "end": v(546.1, 106.12) * mm});
            skLineSegment(sketch, "E203", {"start": v(351.37, -114.3) * mm, "end": v(342.9, -114.3) * mm});
            skLineSegment(sketch, "E204", {"start": v(342.9, -114.3) * mm, "end": v(342.9, -104.7) * mm});
            skLineSegment(sketch, "E205", {"start": v(330.2, -104.72) * mm, "end": v(330.2, -114.3) * mm});
            skLineSegment(sketch, "E206", {"start": v(330.2, -114.3) * mm, "end": v(321.72, -114.3) * mm});
            skLineSegment(sketch, "E207", {"start": v(127, 105.6) * mm, "end": v(127, 115.18) * mm});
            skLineSegment(sketch, "E208", {"start": v(127, 115.18) * mm, "end": v(135.47, 115.2) * mm});
            skSolve(sketch);
        }
        {
            var Q0;
            Q0=qSketchRegion(id+"F32",true);
            extrude(context, id + "F33", {"entities" : qUnion([Q0]), "operationType" : NewBodyOperationType.ADD, "oppositeDirection" : true, "depth" : 12.7 * mm});
        }
        {
            var Q0;
            Q0=qSketchRegion(id+"F29",true);
            var Q1;
            {var subQ7=sQuery(id+"F29.wireOp",EDGE,"E163");Q1=makeQuery(id+"F29.imprint","IMPRINT",FACE,{"disambiguationData":[TD([[makeQuery(id+"F29.imprint","IMPRINT",EDGE,{"derivedFrom":subQ7}),1.0]])]});}
            extrude(context, id + "F34", {"entities" : qUnion([Q0, Q1]), "oppositeDirection" : true, "depth" : 12.7 * mm});
        }
        {
            var Q0;
            Q0=makeQuery(id+"F7.boolean.opBoolean","COPY",FACE,{"derivedFrom":makeQuery(id+"F7.opExtrude","SWEPT_FACE",FACE,{"disambiguationData":[OSD([sQuery(id+"F6.wireOp",EDGE,"E19")])]})});
            var sketch = newSketch(context, id + "F35", { "sketchPlane" : qUnion([Q0])});
            skLineSegment(sketch, "E209", {"start": v(741.5, 76.56) * mm, "end": v(550.02, -82.08) * mm, "construction": true});
            skLineSegment(sketch, "E210", {"start": v(307.48, 89.08) * mm, "end": v(537.26, -82.45) * mm, "construction": true});
            skLineSegment(sketch, "E211", {"start": v(294.72, 89.45) * mm, "end": v(90.47, -95.34) * mm, "construction": true});
            skLineSegment(sketch, "E212", {"start": v(77.7, -95.71) * mm, "end": v(-126.53, 101.6) * mm, "construction": true});
            skLineSegment(sketch, "E213", {"start": v(741.5, 76.56) * mm, "end": v(741.5, 68.32) * mm});
            skLineSegment(sketch, "E214", {"start": v(741.5, 68.32) * mm, "end": v(560.33, -81.79) * mm});
            skLineSegment(sketch, "E215", {"start": v(550.02, -73.84) * mm, "end": v(731.55, 76.56) * mm});
            skLineSegment(sketch, "E216", {"start": v(731.55, 76.56) * mm, "end": v(741.5, 76.56) * mm});
            skLineSegment(sketch, "E217", {"start": v(537.26, -82.45) * mm, "end": v(537.26, -74.53) * mm});
            skLineSegment(sketch, "E218", {"start": v(537.26, -74.53) * mm, "end": v(318.52, 88.76) * mm});
            skLineSegment(sketch, "E219", {"start": v(307.48, 81.15) * mm, "end": v(527.04, -82.75) * mm});
            skLineSegment(sketch, "E220", {"start": v(527.04, -82.75) * mm, "end": v(537.26, -82.45) * mm});
            skLineSegment(sketch, "E221", {"start": v(294.72, 89.45) * mm, "end": v(294.72, 80.88) * mm});
            skLineSegment(sketch, "E222", {"start": v(294.72, 80.88) * mm, "end": v(100.25, -95.05) * mm});
            skLineSegment(sketch, "E223", {"start": v(100.25, -95.05) * mm, "end": v(90.47, -95.34) * mm});
            skLineSegment(sketch, "E224", {"start": v(90.47, -95.34) * mm, "end": v(90.47, -86.77) * mm});
            skLineSegment(sketch, "E225", {"start": v(90.47, -86.77) * mm, "end": v(285.54, 89.71) * mm});
            skLineSegment(sketch, "E226", {"start": v(285.54, 89.71) * mm, "end": v(294.72, 89.45) * mm});
            skLineSegment(sketch, "E227", {"start": v(77.7, -95.71) * mm, "end": v(77.7, -86.88) * mm});
            skLineSegment(sketch, "E228", {"start": v(77.7, -86.88) * mm, "end": v(-117.11, 101.32) * mm});
            skLineSegment(sketch, "E229", {"start": v(-117.11, 101.32) * mm, "end": v(-126.53, 101.6) * mm});
            skLineSegment(sketch, "E230", {"start": v(-126.53, 92.77) * mm, "end": v(68.83, -95.97) * mm});
            skLineSegment(sketch, "E231", {"start": v(68.83, -95.97) * mm, "end": v(77.7, -95.71) * mm});
            skLineSegment(sketch, "E232", {"start": v(550.02, -82.08) * mm, "end": v(560.33, -81.79) * mm});
            skLineSegment(sketch, "E233", {"start": v(307.48, 89.08) * mm, "end": v(318.52, 88.76) * mm});
            skLineSegment(sketch, "E234", {"start": v(-126.53, 92.77) * mm, "end": v(-126.53, 101.6) * mm});
            skSolve(sketch);
        }
        {
            var Q0;
            {var subQ5=sQuery(id+"F4.wireOp",EDGE,"E5.right");var subQ10=sQuery(id+"F0.wireOp",EDGE,"E0.bottom");var subQ18=sQuery(id+"F0.wireOp",EDGE,"E0.top");var subQ21=sQuery(id+"F4.wireOp",EDGE,"E4.right");var subQ40=makeQuery(id+"F1.opExtrude","CAP_FACE",FACE,{"disambiguationData":[OSD([subQ10,subQ18,sQuery(id+"F0.wireOp",EDGE,"E0.left"),sQuery(id+"F0.wireOp",EDGE,"E0.right")])],"isStart":true});Q0=makeQuery(id+"F7.boolean.opBoolean","MERGE",FACE,{"derivedFrom":[makeQuery(id+"F5.boolean.opBoolean","SPLIT",FACE,{"disambiguationData":[TD([makeQuery(id+"F5.opExtrude","SWEPT_FACE",FACE,{"disambiguationData":[OSD([subQ21])]})])],"derivedFrom":subQ40}),makeQuery(id+"F5.boolean.opBoolean","SPLIT",FACE,{"disambiguationData":[TD([makeQuery(id+"F5.opExtrude","SWEPT_FACE",FACE,{"disambiguationData":[OSD([subQ5])]})])],"derivedFrom":subQ40}),makeQuery(id+"F7.opExtrude","SWEPT_FACE",FACE,{"disambiguationData":[OSD([sQuery(id+"F6.wireOp",EDGE,"E25")])]})]});}
            var sketch = newSketch(context, id + "F36", { "sketchPlane" : qUnion([Q0])});
            skLineSegment(sketch, "E235", {"start": v(-127, 101.96) * mm, "end": v(-330.2, -101.6) * mm, "construction": true});
            skLineSegment(sketch, "E236", {"start": v(-546.1, 101.96) * mm, "end": v(-342.9, -101.6) * mm, "construction": true});
            skLineSegment(sketch, "E237", {"start": v(-546.1, 101.96) * mm, "end": v(-546.1, 92.97) * mm});
            skLineSegment(sketch, "E238", {"start": v(-546.1, 92.97) * mm, "end": v(-351.87, -101.6) * mm});
            skLineSegment(sketch, "E239", {"start": v(-351.87, -101.6) * mm, "end": v(-342.9, -101.6) * mm});
            skLineSegment(sketch, "E240", {"start": v(-342.9, -92.61) * mm, "end": v(-537.13, 101.96) * mm});
            skLineSegment(sketch, "E241", {"start": v(-537.13, 101.96) * mm, "end": v(-546.1, 101.96) * mm});
            skLineSegment(sketch, "E242", {"start": v(-330.2, -101.6) * mm, "end": v(-321.23, -101.6) * mm});
            skLineSegment(sketch, "E243", {"start": v(-321.23, -101.6) * mm, "end": v(-127, 92.97) * mm});
            skLineSegment(sketch, "E244", {"start": v(-127, 92.97) * mm, "end": v(-127, 101.96) * mm});
            skLineSegment(sketch, "E245", {"start": v(-135.97, 101.96) * mm, "end": v(-330.2, -92.61) * mm});
            skLineSegment(sketch, "E246", {"start": v(-330.2, -92.61) * mm, "end": v(-330.2, -101.6) * mm});
            skSolve(sketch);
        }
        {
            var Q0;
            Q0=makeQuery(id+"F35.imprint","IMPRINT",FACE,{"disambiguationData":[TD([[makeQuery(id+"F35.imprint","IMPRINT",EDGE,{"derivedFrom":sQuery(id+"F35.wireOp",EDGE,"E221")}),1.0]])]});
            var Q1;
            Q1=makeQuery(id+"F35.imprint","IMPRINT",FACE,{"disambiguationData":[TD([[makeQuery(id+"F35.imprint","IMPRINT",EDGE,{"derivedFrom":sQuery(id+"F35.wireOp",EDGE,"E217")}),1.0]])]});
            var Q2;
            Q2=makeQuery(id+"F35.imprint","IMPRINT",FACE,{"disambiguationData":[TD([[makeQuery(id+"F35.imprint","IMPRINT",EDGE,{"derivedFrom":sQuery(id+"F35.wireOp",EDGE,"E213")}),1.0]])]});
            var Q3;
            Q3=makeQuery(id+"F35.imprint","IMPRINT",FACE,{"disambiguationData":[TD([[makeQuery(id+"F35.imprint","IMPRINT",EDGE,{"derivedFrom":sQuery(id+"F35.wireOp",EDGE,"E227")}),1.0]])]});
            extrude(context, id + "F37", {"entities" : qUnion([Q0, Q1, Q2, Q3]), "oppositeDirection" : true, "depth" : 12.7 * mm});
        }
        {
            var Q0;
            Q0=makeQuery(id+"F36.imprint","IMPRINT",FACE,{"disambiguationData":[TD([[makeQuery(id+"F36.imprint","IMPRINT",EDGE,{"derivedFrom":sQuery(id+"F36.wireOp",EDGE,"E242")}),1.0]])]});
            var Q1;
            Q1=makeQuery(id+"F36.imprint","IMPRINT",FACE,{"disambiguationData":[TD([[makeQuery(id+"F36.imprint","IMPRINT",EDGE,{"derivedFrom":sQuery(id+"F36.wireOp",EDGE,"E237")}),-1.0]])]});
            extrude(context, id + "F38", {"entities" : qUnion([Q0, Q1]), "oppositeDirection" : true, "depth" : 12.7 * mm});
        }
        {
            var Q0;
            {var subQ1=makeQuery(id+"F9.boolean.opBoolean","COPY",FACE,{"derivedFrom":makeQuery(id+"F9.opExtrude","SWEPT_FACE",FACE,{"disambiguationData":[OSD([sQuery(id+"F8.wireOp",EDGE,"E50")])]})});var subQ5=sQuery(id+"F4.wireOp",EDGE,"E11.left");var subQ6=makeQuery(id+"F5.opExtrude","SWEPT_FACE",FACE,{"disambiguationData":[OSD([subQ5])]});var subQ7=sQuery(id+"F4.wireOp",EDGE,"E7.right");var subQ12=sQuery(id+"F4.wireOp",EDGE,"E6.right");var subQ17=sQuery(id+"F4.wireOp",EDGE,"E5.right");var subQ22=sQuery(id+"F0.wireOp",EDGE,"E0.bottom");var subQ30=sQuery(id+"F0.wireOp",EDGE,"E0.top");var subQ33=sQuery(id+"F4.wireOp",EDGE,"E4.right");var subQ45=sQuery(id+"F0.wireOp",EDGE,"E0.left");var subQ46=makeQuery(id+"F1.opExtrude","CAP_FACE",FACE,{"disambiguationData":[OSD([subQ22,subQ30,subQ45,sQuery(id+"F0.wireOp",EDGE,"E0.right")])],"isStart":false});var subQ47=makeQuery(id+"F5.boolean.opBoolean","SPLIT",FACE,{"disambiguationData":[TD([subQ6])],"derivedFrom":subQ46});var subQ48=makeQuery(id+"F9.boolean.opBoolean","COPY",FACE,{"derivedFrom":makeQuery(id+"F9.opExtrude","SWEPT_FACE",FACE,{"disambiguationData":[OSD([sQuery(id+"F8.wireOp",EDGE,"E48")])]})});var subQ50=makeQuery(id+"F5.opExtrude","SWEPT_FACE",FACE,{"disambiguationData":[OSD([subQ7])]});var subQ53=makeQuery(id+"F5.boolean.opBoolean","SPLIT",FACE,{"disambiguationData":[TD([subQ50])],"derivedFrom":subQ46});var subQ57=makeQuery(id+"F5.opExtrude","SWEPT_FACE",FACE,{"disambiguationData":[OSD([subQ12])]});var subQ59=makeQuery(id+"F5.boolean.opBoolean","SPLIT",FACE,{"disambiguationData":[TD([subQ57])],"derivedFrom":subQ46});var subQ62=makeQuery(id+"F5.opExtrude","SWEPT_FACE",FACE,{"disambiguationData":[OSD([subQ17])]});var subQ65=makeQuery(id+"F5.boolean.opBoolean","SPLIT",FACE,{"disambiguationData":[TD([subQ62])],"derivedFrom":subQ46});var subQ67=makeQuery(id+"F5.opExtrude","SWEPT_FACE",FACE,{"disambiguationData":[OSD([subQ33])]});var subQ70=makeQuery(id+"F5.boolean.opBoolean","SPLIT",FACE,{"disambiguationData":[TD([subQ67])],"derivedFrom":subQ46});Q0=makeQuery(id+"F13.boolean.opBoolean","MERGE",FACE,{"derivedFrom":[makeQuery(id+"F5.boolean.opBoolean","SPLIT",FACE,{"disambiguationData":[TD([makeQuery(id+"F1.opExtrude","SWEPT_FACE",FACE,{"disambiguationData":[OSD([subQ45])]})])],"derivedFrom":subQ46}),makeQuery(id+"F11.boolean.opBoolean","SPLIT",FACE,{"disambiguationData":[TD([makeQuery(id+"F11.opExtrude","SWEPT_FACE",FACE,{"disambiguationData":[OSD([sQuery(id+"F10.wireOp",EDGE,"E61")])]})])],"derivedFrom":subQ70}),makeQuery(id+"F11.boolean.opBoolean","SPLIT",FACE,{"disambiguationData":[TD([makeQuery(id+"F11.opExtrude","SWEPT_FACE",FACE,{"disambiguationData":[OSD([sQuery(id+"F10.wireOp",EDGE,"E60")])]})])],"derivedFrom":subQ70}),makeQuery(id+"F11.boolean.opBoolean","SPLIT",FACE,{"disambiguationData":[TD([makeQuery(id+"F11.opExtrude","SWEPT_FACE",FACE,{"disambiguationData":[OSD([sQuery(id+"F10.wireOp",EDGE,"E55.0")])]})])],"derivedFrom":subQ65}),makeQuery(id+"F11.boolean.opBoolean","SPLIT",FACE,{"disambiguationData":[TD([makeQuery(id+"F11.opExtrude","SWEPT_FACE",FACE,{"disambiguationData":[OSD([sQuery(id+"F10.wireOp",EDGE,"E56.0")])]})])],"derivedFrom":subQ65}),makeQuery(id+"F11.boolean.opBoolean","SPLIT",FACE,{"disambiguationData":[TD([subQ48])],"derivedFrom":subQ59}),makeQuery(id+"F11.boolean.opBoolean","SPLIT",FACE,{"disambiguationData":[TD([subQ1])],"derivedFrom":subQ59}),makeQuery(id+"F11.boolean.opBoolean","SPLIT",FACE,{"disambiguationData":[TD([subQ48])],"derivedFrom":subQ53}),makeQuery(id+"F11.boolean.opBoolean","SPLIT",FACE,{"disambiguationData":[TD([subQ1])],"derivedFrom":subQ53}),makeQuery(id+"F11.boolean.opBoolean","SPLIT",FACE,{"disambiguationData":[TD([subQ48])],"derivedFrom":subQ47}),makeQuery(id+"F11.boolean.opBoolean","SPLIT",FACE,{"disambiguationData":[TD([subQ1])],"derivedFrom":subQ47}),makeQuery(id+"F13.opExtrude","SWEPT_FACE",FACE,{"disambiguationData":[OSD([sQuery(id+"F12.wireOp",EDGE,"E99.top")])]})]});}
            var sketch = newSketch(context, id + "F39", { "sketchPlane" : qUnion([Q0])});
            skLineSegment(sketch, "E247", {"start": v(762, 88.9) * mm, "end": v(762, -88.9) * mm});
            skLineSegment(sketch, "E248", {"start": v(762, 88.9) * mm, "end": v(-114.3, 114.3) * mm});
            skLineSegment(sketch, "E249", {"start": v(-114.3, -114.3) * mm, "end": v(762, -88.9) * mm});
            skLineSegment(sketch, "E250", {"start": v(-114.3, -114.3) * mm, "end": v(-114.3, 114.3) * mm});
            skSolve(sketch);
        }
        {
            var Q0;
            Q0=qSketchRegion(id+"F39",true);
            extrude(context, id + "F40", {"entities" : qUnion([Q0]), "depth" : 2.54 * mm});
        }
        {
            var Q0;
            Q0=makeQuery(id+"F1.opExtrude","SWEPT_FACE",FACE,{"disambiguationData":[OSD([sQuery(id+"F0.wireOp",EDGE,"E0.left")])]});
            var sketch = newSketch(context, id + "F41", { "sketchPlane" : qUnion([Q0])});
            skLineSegment(sketch, "E251.bottom", {"start": v(-88.9, 127) * mm, "end": v(88.9, 127) * mm});
            skLineSegment(sketch, "E251.top", {"start": v(-88.9, -38.1) * mm, "end": v(88.9, -38.1) * mm});
            skLineSegment(sketch, "E251.left", {"start": v(-88.9, 127) * mm, "end": v(-88.9, -38.1) * mm});
            skLineSegment(sketch, "E251.right", {"start": v(88.9, 127) * mm, "end": v(88.9, -38.1) * mm});
            skSolve(sketch);
        }
        {
            var Q0;
            Q0=qSketchRegion(id+"F41",true);
            extrude(context, id + "F42", {"entities" : qUnion([Q0]), "depth" : 2.54 * mm});
        }
        {
            var Q0;
            {var subQ1=makeQuery(id+"F9.boolean.opBoolean","COPY",FACE,{"derivedFrom":makeQuery(id+"F9.opExtrude","SWEPT_FACE",FACE,{"disambiguationData":[OSD([sQuery(id+"F8.wireOp",EDGE,"E50")])]})});var subQ5=sQuery(id+"F4.wireOp",EDGE,"E11.left");var subQ6=makeQuery(id+"F5.opExtrude","SWEPT_FACE",FACE,{"disambiguationData":[OSD([subQ5])]});var subQ7=sQuery(id+"F4.wireOp",EDGE,"E7.right");var subQ12=sQuery(id+"F4.wireOp",EDGE,"E6.right");var subQ17=sQuery(id+"F4.wireOp",EDGE,"E5.right");var subQ22=sQuery(id+"F0.wireOp",EDGE,"E0.bottom");var subQ30=sQuery(id+"F0.wireOp",EDGE,"E0.top");var subQ33=sQuery(id+"F4.wireOp",EDGE,"E4.right");var subQ45=sQuery(id+"F0.wireOp",EDGE,"E0.left");var subQ46=makeQuery(id+"F1.opExtrude","CAP_FACE",FACE,{"disambiguationData":[OSD([subQ22,subQ30,subQ45,sQuery(id+"F0.wireOp",EDGE,"E0.right")])],"isStart":false});var subQ47=makeQuery(id+"F5.boolean.opBoolean","SPLIT",FACE,{"disambiguationData":[TD([subQ6])],"derivedFrom":subQ46});var subQ48=makeQuery(id+"F9.boolean.opBoolean","COPY",FACE,{"derivedFrom":makeQuery(id+"F9.opExtrude","SWEPT_FACE",FACE,{"disambiguationData":[OSD([sQuery(id+"F8.wireOp",EDGE,"E48")])]})});var subQ50=makeQuery(id+"F5.opExtrude","SWEPT_FACE",FACE,{"disambiguationData":[OSD([subQ7])]});var subQ53=makeQuery(id+"F5.boolean.opBoolean","SPLIT",FACE,{"disambiguationData":[TD([subQ50])],"derivedFrom":subQ46});var subQ57=makeQuery(id+"F5.opExtrude","SWEPT_FACE",FACE,{"disambiguationData":[OSD([subQ12])]});var subQ59=makeQuery(id+"F5.boolean.opBoolean","SPLIT",FACE,{"disambiguationData":[TD([subQ57])],"derivedFrom":subQ46});var subQ62=makeQuery(id+"F5.opExtrude","SWEPT_FACE",FACE,{"disambiguationData":[OSD([subQ17])]});var subQ65=makeQuery(id+"F5.boolean.opBoolean","SPLIT",FACE,{"disambiguationData":[TD([subQ62])],"derivedFrom":subQ46});var subQ67=makeQuery(id+"F5.opExtrude","SWEPT_FACE",FACE,{"disambiguationData":[OSD([subQ33])]});var subQ70=makeQuery(id+"F5.boolean.opBoolean","SPLIT",FACE,{"disambiguationData":[TD([subQ67])],"derivedFrom":subQ46});Q0=makeQuery(id+"F13.boolean.opBoolean","MERGE",FACE,{"derivedFrom":[makeQuery(id+"F5.boolean.opBoolean","SPLIT",FACE,{"disambiguationData":[TD([makeQuery(id+"F1.opExtrude","SWEPT_FACE",FACE,{"disambiguationData":[OSD([subQ45])]})])],"derivedFrom":subQ46}),makeQuery(id+"F11.boolean.opBoolean","SPLIT",FACE,{"disambiguationData":[TD([makeQuery(id+"F11.opExtrude","SWEPT_FACE",FACE,{"disambiguationData":[OSD([sQuery(id+"F10.wireOp",EDGE,"E61")])]})])],"derivedFrom":subQ70}),makeQuery(id+"F11.boolean.opBoolean","SPLIT",FACE,{"disambiguationData":[TD([makeQuery(id+"F11.opExtrude","SWEPT_FACE",FACE,{"disambiguationData":[OSD([sQuery(id+"F10.wireOp",EDGE,"E60")])]})])],"derivedFrom":subQ70}),makeQuery(id+"F11.boolean.opBoolean","SPLIT",FACE,{"disambiguationData":[TD([makeQuery(id+"F11.opExtrude","SWEPT_FACE",FACE,{"disambiguationData":[OSD([sQuery(id+"F10.wireOp",EDGE,"E55.0")])]})])],"derivedFrom":subQ65}),makeQuery(id+"F11.boolean.opBoolean","SPLIT",FACE,{"disambiguationData":[TD([makeQuery(id+"F11.opExtrude","SWEPT_FACE",FACE,{"disambiguationData":[OSD([sQuery(id+"F10.wireOp",EDGE,"E56.0")])]})])],"derivedFrom":subQ65}),makeQuery(id+"F11.boolean.opBoolean","SPLIT",FACE,{"disambiguationData":[TD([subQ48])],"derivedFrom":subQ59}),makeQuery(id+"F11.boolean.opBoolean","SPLIT",FACE,{"disambiguationData":[TD([subQ1])],"derivedFrom":subQ59}),makeQuery(id+"F11.boolean.opBoolean","SPLIT",FACE,{"disambiguationData":[TD([subQ48])],"derivedFrom":subQ53}),makeQuery(id+"F11.boolean.opBoolean","SPLIT",FACE,{"disambiguationData":[TD([subQ1])],"derivedFrom":subQ53}),makeQuery(id+"F11.boolean.opBoolean","SPLIT",FACE,{"disambiguationData":[TD([subQ48])],"derivedFrom":subQ47}),makeQuery(id+"F11.boolean.opBoolean","SPLIT",FACE,{"disambiguationData":[TD([subQ1])],"derivedFrom":subQ47}),makeQuery(id+"F13.opExtrude","SWEPT_FACE",FACE,{"disambiguationData":[OSD([sQuery(id+"F12.wireOp",EDGE,"E99.top")])]})]});}
            var sketch = newSketch(context, id + "F43", { "sketchPlane" : qUnion([Q0])});
            skLineSegment(sketch, "E252.bottom", {"start": v(-558.8, 114.3) * mm, "end": v(-127, 114.3) * mm});
            skLineSegment(sketch, "E252.top", {"start": v(-558.8, -114.3) * mm, "end": v(-127, -114.3) * mm});
            skLineSegment(sketch, "E252.left", {"start": v(-558.8, 114.3) * mm, "end": v(-558.8, -114.3) * mm});
            skLineSegment(sketch, "E253", {"start": v(-127, 114.3) * mm, "end": v(-114.3, 114.3) * mm});
            skLineSegment(sketch, "E254", {"start": v(-114.3, 114.3) * mm, "end": v(-114.3, -114.3) * mm});
            skLineSegment(sketch, "E255", {"start": v(-114.3, -114.3) * mm, "end": v(-127, -114.3) * mm});
            skSolve(sketch);
        }
        {
            var Q0;
            Q0=qSketchRegion(id+"F43",true);
            extrude(context, id + "F44", {"entities" : qUnion([Q0]), "depth" : 2.54 * mm});
        }
        {
            var Q0;
            Q0=makeQuery(id+"F7.boolean.opBoolean","COPY",FACE,{"derivedFrom":makeQuery(id+"F7.opExtrude","SWEPT_FACE",FACE,{"disambiguationData":[OSD([sQuery(id+"F6.wireOp",EDGE,"E13")])]})});
            var sketch = newSketch(context, id + "F45", { "sketchPlane" : qUnion([Q0])});
            skLineSegment(sketch, "E256", {"start": v(-707.9, 77.57) * mm, "end": v(-494.86, 114.3) * mm});
            skLineSegment(sketch, "E257", {"start": v(-494.86, 114.3) * mm, "end": v(-494.86, -114.3) * mm});
            skLineSegment(sketch, "E258", {"start": v(-494.86, -114.3) * mm, "end": v(-707.9, -77.57) * mm});
            skLineSegment(sketch, "E259", {"start": v(-707.9, -77.57) * mm, "end": v(-707.9, 77.57) * mm});
            skSolve(sketch);
        }
        {
            var Q0;
            Q0=qSketchRegion(id+"F45",true);
            extrude(context, id + "F46", {"entities" : qUnion([Q0]), "depth" : 2.54 * mm});
        }
        {
            var Q0;
            Q0=makeQuery(id+"F1.opExtrude","SWEPT_FACE",FACE,{"disambiguationData":[OSD([sQuery(id+"F0.wireOp",EDGE,"E0.right")])]});
            var sketch = newSketch(context, id + "F47", { "sketchPlane" : qUnion([Q0])});
            skLineSegment(sketch, "E260.bottom", {"start": v(-77.57, 63.02) * mm, "end": v(77.57, 63.02) * mm});
            skLineSegment(sketch, "E260.top", {"start": v(-77.57, -38.1) * mm, "end": v(77.57, -38.1) * mm});
            skLineSegment(sketch, "E260.left", {"start": v(-77.57, 63.02) * mm, "end": v(-77.57, -38.1) * mm});
            skLineSegment(sketch, "E260.right", {"start": v(77.57, 63.02) * mm, "end": v(77.57, -38.1) * mm});
            skSolve(sketch);
        }
        {
            var Q0;
            Q0=qSketchRegion(id+"F47",true);
            extrude(context, id + "F48", {"entities" : qUnion([Q0]), "depth" : 2.54 * mm});
        }
        {
            var Q0;
            Q0=makeQuery(id+"F9.boolean.opBoolean","COPY",FACE,{"derivedFrom":makeQuery(id+"F9.opExtrude","SWEPT_FACE",FACE,{"disambiguationData":[OSD([sQuery(id+"F8.wireOp",EDGE,"E52")])]})});
            var sketch = newSketch(context, id + "F49", { "sketchPlane" : qUnion([Q0])});
            skLineSegment(sketch, "E261", {"start": v(-529.56, -127) * mm, "end": v(-736.05, -38.1) * mm});
            skLineSegment(sketch, "E262", {"start": v(-736.05, -38.1) * mm, "end": v(-736.05, 63.02) * mm});
            skLineSegment(sketch, "E263", {"start": v(-736.05, 63.02) * mm, "end": v(-529.56, 127) * mm});
            skLineSegment(sketch, "E264", {"start": v(-529.56, 127) * mm, "end": v(-529.56, -127) * mm});
            skSolve(sketch);
        }
        {
            var Q0;
            Q0=qSketchRegion(id+"F49",true);
            extrude(context, id + "F50", {"entities" : qUnion([Q0]), "depth" : 2.54 * mm});
        }
        {
            var Q0;
            {var subQ0=sQuery(id+"F8.wireOp",EDGE,"E49");var subQ1=sQuery(id+"F8.wireOp",EDGE,"E46.MirrorCS");Q0=makeQuery(id+"F34.boolean.opBoolean","MERGE",FACE,{"derivedFrom":[makeQuery(id+"F9.boolean.opBoolean","COPY",FACE,{"derivedFrom":makeQuery(id+"F9.opExtrude","SWEPT_FACE",FACE,{"disambiguationData":[OSD([subQ1,subQ0])]})}),makeQuery(id+"F34.opExtrude","CAP_FACE",FACE,{"disambiguationData":[OSD([sQuery(id+"F29.wireOp",EDGE,"E156"),sQuery(id+"F29.wireOp",EDGE,"E157"),sQuery(id+"F29.wireOp",EDGE,"E158"),sQuery(id+"F29.wireOp",EDGE,"E159"),sQuery(id+"F29.wireOp",EDGE,"E160"),sQuery(id+"F29.wireOp",EDGE,"E161")])],"isStart":true}),makeQuery(id+"F34.opExtrude","CAP_FACE",FACE,{"disambiguationData":[OSD([subQ1,subQ0,sQuery(id+"F12.wireOp",EDGE,"E79.3"),sQuery(id+"F12.wireOp",EDGE,"E85.0.1"),sQuery(id+"F29.wireOp",EDGE,"E163"),sQuery(id+"F29.wireOp",EDGE,"E164"),sQuery(id+"F29.wireOp",EDGE,"E165"),sQuery(id+"F29.wireOp",EDGE,"E166")])],"isStart":true})]});}
            var sketch = newSketch(context, id + "F51", { "sketchPlane" : qUnion([Q0])});
            skLineSegment(sketch, "E265.bottom", {"start": v(-114.3, -127) * mm, "end": v(-558.8, -127) * mm});
            skLineSegment(sketch, "E265.top", {"start": v(-114.3, 127) * mm, "end": v(-558.8, 127) * mm});
            skLineSegment(sketch, "E265.left", {"start": v(-114.3, -127) * mm, "end": v(-114.3, 127) * mm});
            skLineSegment(sketch, "E265.right", {"start": v(-558.8, -127) * mm, "end": v(-558.8, 127) * mm});
            skSolve(sketch);
        }
        {
            var Q0;
            Q0=qSketchRegion(id+"F51",true);
            extrude(context, id + "F52", {"entities" : qUnion([Q0]), "depth" : 2.54 * mm});
        }
        {
            var Q0;
            Q0=makeQuery(id+"F9.boolean.opBoolean","COPY",FACE,{"derivedFrom":makeQuery(id+"F9.opExtrude","SWEPT_FACE",FACE,{"disambiguationData":[OSD([sQuery(id+"F8.wireOp",EDGE,"E50")])]})});
            var sketch = newSketch(context, id + "F53", { "sketchPlane" : qUnion([Q0])});
            skLineSegment(sketch, "E266", {"start": v(759.1, 127) * mm, "end": v(-117.56, 127) * mm});
            skLineSegment(sketch, "E267", {"start": v(-117.56, 127) * mm, "end": v(-117.56, -127) * mm});
            skLineSegment(sketch, "E268", {"start": v(-117.56, -127) * mm, "end": v(759.1, -38.1) * mm});
            skLineSegment(sketch, "E269", {"start": v(759.1, -38.1) * mm, "end": v(759.1, 127) * mm});
            skSolve(sketch);
        }
        {
            var Q0;
            Q0=qSketchRegion(id+"F53",true);
            extrude(context, id + "F54", {"entities" : qUnion([Q0]), "depth" : 2.54 * mm});
        }
        {
            var Q0;
            Q0=makeQuery(id+"F9.boolean.opBoolean","COPY",FACE,{"derivedFrom":makeQuery(id+"F9.opExtrude","SWEPT_FACE",FACE,{"disambiguationData":[OSD([sQuery(id+"F8.wireOp",EDGE,"E48")])]})});
            var sketch = newSketch(context, id + "F55", { "sketchPlane" : qUnion([Q0])});
            skLineSegment(sketch, "E270", {"start": v(-759.1, 127) * mm, "end": v(117.56, 127) * mm});
            skLineSegment(sketch, "E271", {"start": v(117.56, 127) * mm, "end": v(117.56, -127) * mm});
            skLineSegment(sketch, "E272", {"start": v(117.56, -127) * mm, "end": v(-759.1, -38.1) * mm});
            skLineSegment(sketch, "E273", {"start": v(-759.1, -38.1) * mm, "end": v(-759.1, 127) * mm});
            skSolve(sketch);
        }
        {
            var Q0;
            Q0=qSketchRegion(id+"F55",true);
            extrude(context, id + "F56", {"entities" : qUnion([Q0]), "depth" : 2.54 * mm});
        }
        {
            var Q0;
            Q0=makeQuery(id+"F33.boolean.opBoolean","MERGE",FACE,{"derivedFrom":[makeQuery(id+"F9.boolean.opBoolean","COPY",FACE,{"derivedFrom":makeQuery(id+"F9.opExtrude","SWEPT_FACE",FACE,{"disambiguationData":[OSD([sQuery(id+"F8.wireOp",EDGE,"E45"),sQuery(id+"F8.wireOp",EDGE,"E47")])]})}),makeQuery(id+"F33.opExtrude","CAP_FACE",FACE,{"disambiguationData":[OSD([sQuery(id+"F32.wireOp",EDGE,"E197.0"),sQuery(id+"F32.wireOp",EDGE,"E198.0"),sQuery(id+"F32.wireOp",EDGE,"E205"),sQuery(id+"F32.wireOp",EDGE,"E206"),sQuery(id+"F32.wireOp",EDGE,"E207"),sQuery(id+"F32.wireOp",EDGE,"E208")])],"isStart":true}),makeQuery(id+"F33.opExtrude","CAP_FACE",FACE,{"disambiguationData":[OSD([sQuery(id+"F32.wireOp",EDGE,"E199.0"),sQuery(id+"F32.wireOp",EDGE,"E200.0"),sQuery(id+"F32.wireOp",EDGE,"E201.0"),sQuery(id+"F32.wireOp",EDGE,"E202"),sQuery(id+"F32.wireOp",EDGE,"E203"),sQuery(id+"F32.wireOp",EDGE,"E204")])],"isStart":true})]});
            var sketch = newSketch(context, id + "F57", { "sketchPlane" : qUnion([Q0])});
            skLineSegment(sketch, "E274.bottom", {"start": v(114.3, 127) * mm, "end": v(558.8, 127) * mm});
            skLineSegment(sketch, "E274.top", {"start": v(114.3, -127) * mm, "end": v(558.8, -127) * mm});
            skLineSegment(sketch, "E274.left", {"start": v(114.3, 127) * mm, "end": v(114.3, -127) * mm});
            skLineSegment(sketch, "E274.right", {"start": v(558.8, 127) * mm, "end": v(558.8, -127) * mm});
            skSolve(sketch);
        }
        {
            var Q0;
            Q0=qSketchRegion(id+"F57",true);
            extrude(context, id + "F58", {"entities" : qUnion([Q0]), "depth" : 2.54 * mm});
        }
        {
            var Q0;
            Q0=makeQuery(id+"F9.boolean.opBoolean","COPY",FACE,{"derivedFrom":makeQuery(id+"F9.opExtrude","SWEPT_FACE",FACE,{"disambiguationData":[OSD([sQuery(id+"F8.wireOp",EDGE,"E51")])]})});
            var sketch = newSketch(context, id + "F59", { "sketchPlane" : qUnion([Q0])});
            skLineSegment(sketch, "E275", {"start": v(736.05, 63.02) * mm, "end": v(529.56, 127) * mm});
            skLineSegment(sketch, "E276", {"start": v(529.56, 127) * mm, "end": v(529.56, -127) * mm});
            skLineSegment(sketch, "E277", {"start": v(529.56, -127) * mm, "end": v(736.05, -38.1) * mm});
            skLineSegment(sketch, "E278", {"start": v(736.05, -38.1) * mm, "end": v(736.05, 63.02) * mm});
            skSolve(sketch);
        }
        {
            var Q0;
            Q0=qSketchRegion(id+"F59",true);
            extrude(context, id + "F60", {"entities" : qUnion([Q0]), "depth" : 2.54 * mm});
        }
        {
            var Q0;
            Q0=makeQuery(id+"F7.boolean.opBoolean","COPY",FACE,{"derivedFrom":makeQuery(id+"F7.opExtrude","SWEPT_FACE",FACE,{"disambiguationData":[OSD([sQuery(id+"F6.wireOp",EDGE,"E18")])]})});
            var sketch = newSketch(context, id + "F61", { "sketchPlane" : qUnion([Q0])});
            skLineSegment(sketch, "E279", {"start": v(-682.84, -77.57) * mm, "end": v(-461.04, -114.3) * mm});
            skLineSegment(sketch, "E280", {"start": v(-461.04, -114.3) * mm, "end": v(-461.04, 114.3) * mm});
            skLineSegment(sketch, "E281", {"start": v(-461.04, 114.3) * mm, "end": v(-682.84, 77.57) * mm});
            skLineSegment(sketch, "E282", {"start": v(-682.84, 77.57) * mm, "end": v(-682.84, -77.57) * mm});
            skSolve(sketch);
        }
        {
            var Q0;
            Q0=qSketchRegion(id+"F61",true);
            extrude(context, id + "F62", {"entities" : qUnion([Q0]), "depth" : 2.54 * mm});
        }
        {
            var Q0;
            {var subQ5=sQuery(id+"F4.wireOp",EDGE,"E5.right");var subQ10=sQuery(id+"F0.wireOp",EDGE,"E0.bottom");var subQ18=sQuery(id+"F0.wireOp",EDGE,"E0.top");var subQ21=sQuery(id+"F4.wireOp",EDGE,"E4.right");var subQ40=makeQuery(id+"F1.opExtrude","CAP_FACE",FACE,{"disambiguationData":[OSD([subQ10,subQ18,sQuery(id+"F0.wireOp",EDGE,"E0.left"),sQuery(id+"F0.wireOp",EDGE,"E0.right")])],"isStart":true});Q0=makeQuery(id+"F7.boolean.opBoolean","MERGE",FACE,{"derivedFrom":[makeQuery(id+"F5.boolean.opBoolean","SPLIT",FACE,{"disambiguationData":[TD([makeQuery(id+"F5.opExtrude","SWEPT_FACE",FACE,{"disambiguationData":[OSD([subQ21])]})])],"derivedFrom":subQ40}),makeQuery(id+"F5.boolean.opBoolean","SPLIT",FACE,{"disambiguationData":[TD([makeQuery(id+"F5.opExtrude","SWEPT_FACE",FACE,{"disambiguationData":[OSD([subQ5])]})])],"derivedFrom":subQ40}),makeQuery(id+"F7.opExtrude","SWEPT_FACE",FACE,{"disambiguationData":[OSD([sQuery(id+"F6.wireOp",EDGE,"E25")])]})]});}
            var sketch = newSketch(context, id + "F63", { "sketchPlane" : qUnion([Q0])});
            skLineSegment(sketch, "E283.bottom", {"start": v(-114.3, -114.3) * mm, "end": v(-558.8, -114.3) * mm});
            skLineSegment(sketch, "E283.top", {"start": v(-114.3, 114.3) * mm, "end": v(-558.8, 114.3) * mm});
            skLineSegment(sketch, "E283.left", {"start": v(-114.3, -114.3) * mm, "end": v(-114.3, 114.3) * mm});
            skLineSegment(sketch, "E283.right", {"start": v(-558.8, -114.3) * mm, "end": v(-558.8, 114.3) * mm});
            skSolve(sketch);
        }
        {
            var Q0;
            Q0=qSketchRegion(id+"F63",true);
            extrude(context, id + "F64", {"entities" : qUnion([Q0]), "depth" : 2.54 * mm});
        }
        {
            var Q0;
            Q0=makeQuery(id+"F7.boolean.opBoolean","COPY",FACE,{"derivedFrom":makeQuery(id+"F7.opExtrude","SWEPT_FACE",FACE,{"disambiguationData":[OSD([sQuery(id+"F6.wireOp",EDGE,"E19")])]})});
            var sketch = newSketch(context, id + "F65", { "sketchPlane" : qUnion([Q0])});
            skLineSegment(sketch, "E284", {"start": v(754.26, -88.9) * mm, "end": v(-126.53, -114.3) * mm});
            skLineSegment(sketch, "E285", {"start": v(-126.53, -114.3) * mm, "end": v(-126.53, 114.3) * mm});
            skLineSegment(sketch, "E286", {"start": v(-126.53, 114.3) * mm, "end": v(754.26, 88.9) * mm});
            skLineSegment(sketch, "E287", {"start": v(754.26, 88.9) * mm, "end": v(754.26, -88.9) * mm});
            skSolve(sketch);
        }
        {
            var Q0;
            Q0=qSketchRegion(id+"F65",true);
            extrude(context, id + "F66", {"entities" : qUnion([Q0]), "depth" : 2.54 * mm});
        }
        {
            var Q0;
            Q0=makeQuery(id+"F66.opExtrude","SWEPT_BODY",BODY,{"disambiguationData":[OSD([sQuery(id+"F65.wireOp",EDGE,"E284"),sQuery(id+"F65.wireOp",EDGE,"E285"),sQuery(id+"F65.wireOp",EDGE,"E286"),sQuery(id+"F65.wireOp",EDGE,"E287")])]});
            var Q1;
            Q1=makeQuery(id+"F40.opExtrude","SWEPT_BODY",BODY,{"disambiguationData":[OSD([sQuery(id+"F39.wireOp",EDGE,"E247"),sQuery(id+"F39.wireOp",EDGE,"E248"),sQuery(id+"F39.wireOp",EDGE,"E249"),sQuery(id+"F39.wireOp",EDGE,"E250")])]});
            var Q2;
            Q2=makeQuery(id+"F42.opExtrude","SWEPT_BODY",BODY,{"disambiguationData":[OSD([sQuery(id+"F41.wireOp",EDGE,"E251.bottom"),sQuery(id+"F41.wireOp",EDGE,"E251.top"),sQuery(id+"F41.wireOp",EDGE,"E251.left"),sQuery(id+"F41.wireOp",EDGE,"E251.right")])]});
            var Q3;
            Q3=makeQuery(id+"F44.opExtrude","SWEPT_BODY",BODY,{"disambiguationData":[OSD([sQuery(id+"F43.wireOp",EDGE,"E252.bottom"),sQuery(id+"F43.wireOp",EDGE,"E252.top"),sQuery(id+"F43.wireOp",EDGE,"E252.left"),sQuery(id+"F43.wireOp",EDGE,"E253"),sQuery(id+"F43.wireOp",EDGE,"E254"),sQuery(id+"F43.wireOp",EDGE,"E255")])]});
            var Q4;
            Q4=makeQuery(id+"F46.opExtrude","SWEPT_BODY",BODY,{"disambiguationData":[OSD([sQuery(id+"F45.wireOp",EDGE,"E256"),sQuery(id+"F45.wireOp",EDGE,"E257"),sQuery(id+"F45.wireOp",EDGE,"E258"),sQuery(id+"F45.wireOp",EDGE,"E259")])]});
            var Q5;
            Q5=makeQuery(id+"F48.opExtrude","SWEPT_BODY",BODY,{"disambiguationData":[OSD([sQuery(id+"F47.wireOp",EDGE,"E260.bottom"),sQuery(id+"F47.wireOp",EDGE,"E260.top"),sQuery(id+"F47.wireOp",EDGE,"E260.left"),sQuery(id+"F47.wireOp",EDGE,"E260.right")])]});
            var Q6;
            Q6=makeQuery(id+"F50.opExtrude","SWEPT_BODY",BODY,{"disambiguationData":[OSD([sQuery(id+"F49.wireOp",EDGE,"E261"),sQuery(id+"F49.wireOp",EDGE,"E262"),sQuery(id+"F49.wireOp",EDGE,"E263"),sQuery(id+"F49.wireOp",EDGE,"E264")])]});
            var Q7;
            Q7=makeQuery(id+"F52.opExtrude","SWEPT_BODY",BODY,{"disambiguationData":[OSD([sQuery(id+"F51.wireOp",EDGE,"E265.bottom"),sQuery(id+"F51.wireOp",EDGE,"E265.top"),sQuery(id+"F51.wireOp",EDGE,"E265.left"),sQuery(id+"F51.wireOp",EDGE,"E265.right")])]});
            var Q8;
            Q8=makeQuery(id+"F54.opExtrude","SWEPT_BODY",BODY,{"disambiguationData":[OSD([sQuery(id+"F53.wireOp",EDGE,"E266"),sQuery(id+"F53.wireOp",EDGE,"E267"),sQuery(id+"F53.wireOp",EDGE,"E268"),sQuery(id+"F53.wireOp",EDGE,"E269")])]});
            var Q9;
            Q9=makeQuery(id+"F56.opExtrude","SWEPT_BODY",BODY,{"disambiguationData":[OSD([sQuery(id+"F55.wireOp",EDGE,"E270"),sQuery(id+"F55.wireOp",EDGE,"E271"),sQuery(id+"F55.wireOp",EDGE,"E272"),sQuery(id+"F55.wireOp",EDGE,"E273")])]});
            var Q10;
            Q10=makeQuery(id+"F58.opExtrude","SWEPT_BODY",BODY,{"disambiguationData":[OSD([sQuery(id+"F57.wireOp",EDGE,"E274.bottom"),sQuery(id+"F57.wireOp",EDGE,"E274.top"),sQuery(id+"F57.wireOp",EDGE,"E274.left"),sQuery(id+"F57.wireOp",EDGE,"E274.right")])]});
            var Q11;
            Q11=makeQuery(id+"F60.opExtrude","SWEPT_BODY",BODY,{"disambiguationData":[OSD([sQuery(id+"F59.wireOp",EDGE,"E275"),sQuery(id+"F59.wireOp",EDGE,"E276"),sQuery(id+"F59.wireOp",EDGE,"E277"),sQuery(id+"F59.wireOp",EDGE,"E278")])]});
            var Q12;
            Q12=makeQuery(id+"F62.opExtrude","SWEPT_BODY",BODY,{"disambiguationData":[OSD([sQuery(id+"F61.wireOp",EDGE,"E279"),sQuery(id+"F61.wireOp",EDGE,"E280"),sQuery(id+"F61.wireOp",EDGE,"E281"),sQuery(id+"F61.wireOp",EDGE,"E282")])]});
            var Q13;
            Q13=makeQuery(id+"F64.opExtrude","SWEPT_BODY",BODY,{"disambiguationData":[OSD([sQuery(id+"F63.wireOp",EDGE,"E283.bottom"),sQuery(id+"F63.wireOp",EDGE,"E283.top"),sQuery(id+"F63.wireOp",EDGE,"E283.left"),sQuery(id+"F63.wireOp",EDGE,"E283.right")])]});
            deleteBodies(context, id + "F67", {"entities" : qUnion([Q0, Q1, Q2, Q3, Q4, Q5, Q6, Q7, Q8, Q9, Q10, Q11, Q12, Q13])});
        }
        {
            var Q0;
            Q0=makeQuery(id+"F31.opExtrude","SWEPT_BODY",BODY,{"disambiguationData":[OSD([sQuery(id+"F28.wireOp",EDGE,"E120"),sQuery(id+"F28.wireOp",EDGE,"E124.MirrorCS"),sQuery(id+"F28.wireOp",EDGE,"E132"),sQuery(id+"F28.wireOp",EDGE,"E151"),sQuery(id+"F28.wireOp",EDGE,"E152"),sQuery(id+"F28.wireOp",EDGE,"E153"),sQuery(id+"F28.wireOp",EDGE,"E154")])]});
            deleteBodies(context, id + "F68", {"entities" : qUnion([Q0])});
        }
        {
            var Q0;
            Q0=makeQuery(id+"F38.opExtrude","SWEPT_BODY",BODY,{"disambiguationData":[OSD([sQuery(id+"F0.wireOp",EDGE,"E0.bottom"),sQuery(id+"F0.wireOp",EDGE,"E0.top"),sQuery(id+"F0.wireOp",EDGE,"E0.left"),sQuery(id+"F0.wireOp",EDGE,"E0.right"),sQuery(id+"F6.wireOp",EDGE,"E25"),sQuery(id+"F10.wireOp",EDGE,"E56.0"),sQuery(id+"F36.wireOp",EDGE,"E242"),sQuery(id+"F36.wireOp",EDGE,"E243"),sQuery(id+"F36.wireOp",EDGE,"E244"),sQuery(id+"F36.wireOp",EDGE,"E245"),sQuery(id+"F36.wireOp",EDGE,"E246")])]});
            deleteBodies(context, id + "F69", {"entities" : qUnion([Q0])});
        }
        {
            var Q0;
            Q0=makeQuery(id+"F31.opExtrude","SWEPT_BODY",BODY,{"disambiguationData":[OSD([sQuery(id+"F28.wireOp",EDGE,"E121"),sQuery(id+"F28.wireOp",EDGE,"E125.MirrorCS"),sQuery(id+"F28.wireOp",EDGE,"E133"),sQuery(id+"F28.wireOp",EDGE,"E147"),sQuery(id+"F28.wireOp",EDGE,"E148"),sQuery(id+"F28.wireOp",EDGE,"E149"),sQuery(id+"F28.wireOp",EDGE,"E150")])]});
            deleteBodies(context, id + "F70", {"entities" : qUnion([Q0])});
        }
        {
            var Q0;
            Q0=makeQuery(id+"F31.opExtrude","SWEPT_BODY",BODY,{"disambiguationData":[OSD([sQuery(id+"F28.wireOp",EDGE,"E122"),sQuery(id+"F28.wireOp",EDGE,"E126.MirrorCS"),sQuery(id+"F28.wireOp",EDGE,"E135"),sQuery(id+"F28.wireOp",EDGE,"E136"),sQuery(id+"F28.wireOp",EDGE,"E143"),sQuery(id+"F28.wireOp",EDGE,"E144"),sQuery(id+"F28.wireOp",EDGE,"E145"),sQuery(id+"F28.wireOp",EDGE,"E146")])]});
            deleteBodies(context, id + "F71", {"entities" : qUnion([Q0])});
        }
        {
            var Q0;
            Q0=makeQuery(id+"F31.opExtrude","SWEPT_BODY",BODY,{"disambiguationData":[OSD([sQuery(id+"F28.wireOp",EDGE,"E123"),sQuery(id+"F28.wireOp",EDGE,"E127.MirrorCS"),sQuery(id+"F28.wireOp",EDGE,"E138"),sQuery(id+"F28.wireOp",EDGE,"E139"),sQuery(id+"F28.wireOp",EDGE,"E140"),sQuery(id+"F28.wireOp",EDGE,"E141"),sQuery(id+"F28.wireOp",EDGE,"E142")])]});
            deleteBodies(context, id + "F72", {"entities" : qUnion([Q0])});
        }
        {
            var Q0;
            Q0=makeQuery(id+"F34.opExtrude","SWEPT_BODY",BODY,{"disambiguationData":[OSD([sQuery(id+"F29.wireOp",EDGE,"E156"),sQuery(id+"F29.wireOp",EDGE,"E157"),sQuery(id+"F29.wireOp",EDGE,"E158"),sQuery(id+"F29.wireOp",EDGE,"E159"),sQuery(id+"F29.wireOp",EDGE,"E160"),sQuery(id+"F29.wireOp",EDGE,"E161")])]});
            deleteBodies(context, id + "F73", {"entities" : qUnion([Q0])});
        }
        {
            var Q0;
            Q0=makeQuery(id+"F34.opExtrude","SWEPT_BODY",BODY,{"disambiguationData":[OSD([sQuery(id+"F8.wireOp",EDGE,"E46.MirrorCS"),sQuery(id+"F8.wireOp",EDGE,"E49"),sQuery(id+"F12.wireOp",EDGE,"E79.3"),sQuery(id+"F12.wireOp",EDGE,"E85.0.1"),sQuery(id+"F29.wireOp",EDGE,"E163"),sQuery(id+"F29.wireOp",EDGE,"E164"),sQuery(id+"F29.wireOp",EDGE,"E165"),sQuery(id+"F29.wireOp",EDGE,"E166")])]});
            deleteBodies(context, id + "F74", {"entities" : qUnion([Q0])});
        }
        {
            var Q0;
            Q0=makeQuery(id+"F37.opExtrude","SWEPT_BODY",BODY,{"disambiguationData":[OSD([sQuery(id+"F6.wireOp",EDGE,"E19"),sQuery(id+"F10.wireOp",EDGE,"E66.0.3"),sQuery(id+"F35.wireOp",EDGE,"E213"),sQuery(id+"F35.wireOp",EDGE,"E214"),sQuery(id+"F35.wireOp",EDGE,"E215"),sQuery(id+"F35.wireOp",EDGE,"E216"),sQuery(id+"F35.wireOp",EDGE,"E232")])]});
            deleteBodies(context, id + "F75", {"entities" : qUnion([Q0])});
        }
        {
            var Q0;
            Q0=makeQuery(id+"F37.opExtrude","SWEPT_BODY",BODY,{"disambiguationData":[OSD([sQuery(id+"F6.wireOp",EDGE,"E19"),sQuery(id+"F10.wireOp",EDGE,"E65.0.3"),sQuery(id+"F35.wireOp",EDGE,"E217"),sQuery(id+"F35.wireOp",EDGE,"E218"),sQuery(id+"F35.wireOp",EDGE,"E219"),sQuery(id+"F35.wireOp",EDGE,"E220"),sQuery(id+"F35.wireOp",EDGE,"E233")])]});
            deleteBodies(context, id + "F76", {"entities" : qUnion([Q0])});
        }
        {
            var Q0;
            Q0=makeQuery(id+"F37.opExtrude","SWEPT_BODY",BODY,{"disambiguationData":[OSD([sQuery(id+"F35.wireOp",EDGE,"E221"),sQuery(id+"F35.wireOp",EDGE,"E222"),sQuery(id+"F35.wireOp",EDGE,"E223"),sQuery(id+"F35.wireOp",EDGE,"E224"),sQuery(id+"F35.wireOp",EDGE,"E225"),sQuery(id+"F35.wireOp",EDGE,"E226")])]});
            deleteBodies(context, id + "F77", {"entities" : qUnion([Q0])});
        }
        {
            var Q0;
            Q0=makeQuery(id+"F37.opExtrude","SWEPT_BODY",BODY,{"disambiguationData":[OSD([sQuery(id+"F35.wireOp",EDGE,"E227"),sQuery(id+"F35.wireOp",EDGE,"E228"),sQuery(id+"F35.wireOp",EDGE,"E230"),sQuery(id+"F35.wireOp",EDGE,"E231"),sQuery(id+"F35.wireOp",EDGE,"E234"),sQuery(id+"F35.wireOp",EDGE,"E229")])]});
            deleteBodies(context, id + "F78", {"entities" : qUnion([Q0])});
        }
        {
            var Q0;
            Q0=makeQuery(id+"F38.opExtrude","SWEPT_BODY",BODY,{"disambiguationData":[OSD([sQuery(id+"F0.wireOp",EDGE,"E0.bottom"),sQuery(id+"F0.wireOp",EDGE,"E0.top"),sQuery(id+"F0.wireOp",EDGE,"E0.left"),sQuery(id+"F0.wireOp",EDGE,"E0.right"),sQuery(id+"F6.wireOp",EDGE,"E25"),sQuery(id+"F10.wireOp",EDGE,"E63.0.1"),sQuery(id+"F36.wireOp",EDGE,"E237"),sQuery(id+"F36.wireOp",EDGE,"E238"),sQuery(id+"F36.wireOp",EDGE,"E239"),sQuery(id+"F36.wireOp",EDGE,"E240"),sQuery(id+"F36.wireOp",EDGE,"E241")])]});
            deleteBodies(context, id + "F79", {"entities" : qUnion([Q0])});
        }
        {
            var Q0;
            Q0=makeQuery(id+"F9.boolean.opBoolean","COPY",FACE,{"derivedFrom":makeQuery(id+"F9.opExtrude","SWEPT_FACE",FACE,{"disambiguationData":[OSD([sQuery(id+"F8.wireOp",EDGE,"E48")])]})});
            var sketch = newSketch(context, id + "F80", { "sketchPlane" : qUnion([Q0])});
            skLineSegment(sketch, "E288", {"start": v(-746.4, 114.3) * mm, "end": v(-555.82, -45.95) * mm, "construction": true});
            skLineSegment(sketch, "E289", {"start": v(-314.42, 114.61) * mm, "end": v(-543.11, -48.1) * mm, "construction": true});
            skLineSegment(sketch, "E290", {"start": v(-301.71, 114.63) * mm, "end": v(-98.43, -92.46) * mm, "construction": true});
            skLineSegment(sketch, "E291", {"start": v(-98.43, -92.46) * mm, "end": v(-102.51, -86.96) * mm, "construction": true});
            skLineSegment(sketch, "E292", {"start": v(-85.72, -93.75) * mm, "end": v(117.56, 115.18) * mm, "construction": true});
            skLineSegment(sketch, "E293", {"start": v(-736.53, 114.3) * mm, "end": v(-555.82, -37.65) * mm});
            skLineSegment(sketch, "E294", {"start": v(-543.11, -40.3) * mm, "end": v(-325.4, 114.6) * mm});
            skLineSegment(sketch, "E295.MirrorCS", {"start": v(-744.7, 104.58) * mm, "end": v(-564, -47.37) * mm});
            skLineSegment(sketch, "E296.MirrorCS", {"start": v(-535.75, -50.66) * mm, "end": v(-318.03, 104.25) * mm});
            skLineSegment(sketch, "E297", {"start": v(-744.7, 104.58) * mm, "end": v(-747.1, 106.6) * mm});
            skLineSegment(sketch, "E298", {"start": v(-747.1, 106.6) * mm, "end": v(-746.4, 114.3) * mm});
            skLineSegment(sketch, "E299", {"start": v(-564, -47.37) * mm, "end": v(-552.64, -48.52) * mm});
            skLineSegment(sketch, "E300", {"start": v(-552.64, -48.52) * mm, "end": v(-555.82, -37.65) * mm});
            skLineSegment(sketch, "E301", {"start": v(-543.11, -40.3) * mm, "end": v(-545.46, -50.4) * mm});
            skLineSegment(sketch, "E302", {"start": v(-545.46, -50.4) * mm, "end": v(-535.75, -50.66) * mm});
            skLineSegment(sketch, "E303", {"start": v(-318.03, 104.25) * mm, "end": v(-311.38, 108.98) * mm});
            skLineSegment(sketch, "E304", {"start": v(-311.38, 108.98) * mm, "end": v(-312.6, 117.02) * mm});
            skLineSegment(sketch, "E305", {"start": v(-312.6, 117.02) * mm, "end": v(-325.4, 114.6) * mm});
            skSolve(sketch);
        }
        {
            var Q0;
            Q0 = qSketchRegion(id + "F80", true);
            extrude(context, id + "F81", {"entities" : qUnion([Q0]), "operationType" : NewBodyOperationType.ADD, "oppositeDirection" : true, "depth" : 12.7 * mm});
        }
        {
            var Q0;
            Q0=makeQuery(id+"F81.boolean.opBoolean","MERGE",FACE,{"derivedFrom":[makeQuery(id+"F9.boolean.opBoolean","COPY",FACE,{"derivedFrom":makeQuery(id+"F9.opExtrude","SWEPT_FACE",FACE,{"disambiguationData":[OSD([sQuery(id+"F8.wireOp",EDGE,"E48")])]})}),makeQuery(id+"F81.opExtrude","CAP_FACE",FACE,{"disambiguationData":[OSD([sQuery(id+"F80.wireOp",EDGE,"E294"),sQuery(id+"F80.wireOp",EDGE,"E296.MirrorCS"),sQuery(id+"F80.wireOp",EDGE,"E301"),sQuery(id+"F80.wireOp",EDGE,"E302"),sQuery(id+"F80.wireOp",EDGE,"E303"),sQuery(id+"F80.wireOp",EDGE,"E304"),sQuery(id+"F80.wireOp",EDGE,"E305")])],"isStart":true})]});
            var sketch = newSketch(context, id + "F82", { "sketchPlane" : qUnion([Q0])});
            skLineSegment(sketch, "E306", {"start": v(-98.43, 114.89) * mm, "end": v(-301.71, -71.84) * mm, "construction": true});
            skLineSegment(sketch, "E307", {"start": v(-301.71, 114.63) * mm, "end": v(-98.43, -92.46) * mm, "construction": true});
            skLineSegment(sketch, "E308", {"start": v(-98.43, -92.46) * mm, "end": v(-85.72, -93.75) * mm, "construction": true});
            skLineSegment(sketch, "E309", {"start": v(-85.72, -93.75) * mm, "end": v(117.56, 115.18) * mm, "construction": true});
            skLineSegment(sketch, "E310", {"start": v(-555.82, 114.3) * mm, "end": v(-555.82, -45.95) * mm, "construction": true});
            skLineSegment(sketch, "E311", {"start": v(-555.82, -45.95) * mm, "end": v(-746.4, 114.3) * mm, "construction": true});
            skLineSegment(sketch, "E312", {"start": v(-746.4, 114.3) * mm, "end": v(-736.53, 114.3) * mm});
            skLineSegment(sketch, "E313", {"start": v(-736.53, 114.3) * mm, "end": v(-555.82, -37.65) * mm});
            skLineSegment(sketch, "E314", {"start": v(-555.82, -37.65) * mm, "end": v(-555.82, -45.95) * mm});
            skLineSegment(sketch, "E315.MirrorCS", {"start": v(-744.7, 104.58) * mm, "end": v(-564, -47.37) * mm});
            skLineSegment(sketch, "E316.MirrorCS", {"start": v(-564, -47.37) * mm, "end": v(-555.82, -45.95) * mm});
            skPoint(sketch, "E317.MirrorCS.end.orphan", {"position": v(-744.7, 104.58) * mm});
            skPoint(sketch, "E317.MirrorCS.start.orphan", {"position": v(-746.4, 114.3) * mm});
            skLineSegment(sketch, "E318", {"start": v(-744.7, 104.58) * mm, "end": v(-746.4, 106) * mm});
            skLineSegment(sketch, "E319", {"start": v(-746.4, 106) * mm, "end": v(-746.4, 114.3) * mm});
            skLineSegment(sketch, "E320", {"start": v(-301.71, 114.63) * mm, "end": v(-292.83, 114.64) * mm});
            skLineSegment(sketch, "E321", {"start": v(-292.83, 114.64) * mm, "end": v(-98.43, -83.4) * mm});
            skLineSegment(sketch, "E322", {"start": v(-98.43, -83.4) * mm, "end": v(-98.43, -92.46) * mm});
            skLineSegment(sketch, "E323.MirrorCS", {"start": v(-301.89, 105.74) * mm, "end": v(-107.5, -92.29) * mm});
            skLineSegment(sketch, "E324", {"start": v(-301.89, 105.74) * mm, "end": v(-301.71, 114.63) * mm});
            skLineSegment(sketch, "E325", {"start": v(-107.5, -92.29) * mm, "end": v(-98.43, -92.46) * mm});
            skLineSegment(sketch, "E326", {"start": v(117.56, 115.18) * mm, "end": v(108.7, 115.17) * mm});
            skLineSegment(sketch, "E327", {"start": v(108.7, 115.17) * mm, "end": v(-85.72, -84.64) * mm});
            skLineSegment(sketch, "E328", {"start": v(-85.72, -84.64) * mm, "end": v(-85.72, -93.75) * mm});
            skLineSegment(sketch, "E329.MirrorCS", {"start": v(117.8, 106.31) * mm, "end": v(-76.62, -93.5) * mm});
            skLineSegment(sketch, "E330", {"start": v(-76.62, -93.5) * mm, "end": v(-77.66, -94.56) * mm});
            skLineSegment(sketch, "E331", {"start": v(-77.66, -94.56) * mm, "end": v(-85.72, -93.75) * mm});
            skLineSegment(sketch, "E332", {"start": v(117.8, 106.31) * mm, "end": v(117.56, 115.18) * mm});
            skSolve(sketch);
        }
        {
            var Q0;
            Q0 = qSketchRegion(id + "F82", true);
            extrude(context, id + "F83", {"entities" : qUnion([Q0]), "operationType" : NewBodyOperationType.ADD, "oppositeDirection" : true, "depth" : 12.7 * mm, "hasDraft" : true, "draftAngle" : 3 * degree});
        }
        {
            var Q0;
            Q0=makeQuery(id+"F29.imprint","IMPRINT",FACE,{"disambiguationData":[TD([[makeQuery(id+"F29.imprint","IMPRINT",EDGE,{"derivedFrom":sQuery(id+"F29.wireOp",EDGE,"E156")}),1.0]])]});
            var Q1;
            {var subQ7=sQuery(id+"F29.wireOp",EDGE,"E163");Q1=makeQuery(id+"F29.imprint","IMPRINT",FACE,{"disambiguationData":[TD([[makeQuery(id+"F29.imprint","IMPRINT",EDGE,{"derivedFrom":subQ7}),1.0]])]});}
            extrude(context, id + "F84", {"entities" : qUnion([Q0, Q1]), "operationType" : NewBodyOperationType.ADD, "oppositeDirection" : true, "depth" : 12.7 * mm, "hasDraft" : true, "draftAngle" : 3 * degree});
        }
        {
            var Q0;
            Q0 = qSketchRegion(id + "F28", true);
            extrude(context, id + "F85", {"entities" : qUnion([Q0]), "operationType" : NewBodyOperationType.ADD, "oppositeDirection" : true, "depth" : 12.7 * mm, "hasDraft" : true, "draftAngle" : 3 * degree});
        }
        {
            var Q0;
            Q0 = qSketchRegion(id + "F35", true);
            var Q1;
            Q1=makeQuery(id+"F35.imprint","IMPRINT",FACE,{"disambiguationData":[TD([[makeQuery(id+"F35.imprint","IMPRINT",EDGE,{"derivedFrom":sQuery(id+"F35.wireOp",EDGE,"E217")}),1.0]])]});
            var Q2;
            Q2=makeQuery(id+"F35.imprint","IMPRINT",FACE,{"disambiguationData":[TD([[makeQuery(id+"F35.imprint","IMPRINT",EDGE,{"derivedFrom":sQuery(id+"F35.wireOp",EDGE,"E213")}),1.0]])]});
            extrude(context, id + "F86", {"entities" : qUnion([Q0, Q1, Q2]), "operationType" : NewBodyOperationType.ADD, "oppositeDirection" : true, "depth" : 12.7 * mm, "hasDraft" : true, "draftAngle" : 6 * degree});
        }
        {
            var Q0;
            Q0=makeQuery(id+"F36.imprint","IMPRINT",FACE,{"disambiguationData":[TD([[makeQuery(id+"F36.imprint","IMPRINT",EDGE,{"derivedFrom":sQuery(id+"F36.wireOp",EDGE,"E237")}),-1.0]])]});
            var Q1;
            Q1=makeQuery(id+"F36.imprint","IMPRINT",FACE,{"disambiguationData":[TD([[makeQuery(id+"F36.imprint","IMPRINT",EDGE,{"derivedFrom":sQuery(id+"F36.wireOp",EDGE,"E242")}),1.0]])]});
            extrude(context, id + "F87", {"entities" : qUnion([Q0, Q1]), "operationType" : NewBodyOperationType.ADD, "oppositeDirection" : true, "depth" : 12.7 * mm, "hasDraft" : true, "draftAngle" : 3 * degree});
        }
        {
            var Q0;
            Q0=makeQuery(id+"F1.opExtrude","SWEPT_FACE",FACE,{"disambiguationData":[OSD([sQuery(id+"F0.wireOp",EDGE,"E0.right")])]});
            var sketch = newSketch(context, id + "F88", { "sketchPlane" : qUnion([Q0])});
            skLineSegment(sketch, "E333.bottom", {"start": v(-64.87, 50.32) * mm, "end": v(64.87, 50.32) * mm});
            skLineSegment(sketch, "E333.top", {"start": v(-64.87, -25.4) * mm, "end": v(64.87, -25.4) * mm});
            skLineSegment(sketch, "E333.left", {"start": v(-64.87, 50.32) * mm, "end": v(-64.87, -25.4) * mm});
            skLineSegment(sketch, "E333.right", {"start": v(64.87, 50.32) * mm, "end": v(64.87, -25.4) * mm});
            skSolve(sketch);
        }
        {
            var Q0;
            Q0 = qSketchRegion(id + "F88", true);
            extrude(context, id + "F89", {"entities" : qUnion([Q0]), "operationType" : NewBodyOperationType.REMOVE, "oppositeDirection" : true, "depth" : 25.4 * mm});
        }
        {
            var Q0;
            Q0=qCreatedBy(makeId("Front.planeOp"),FACE);
            var sketch = newSketch(context, id + "F90", { "sketchPlane" : qUnion([Q0])});
            skPoint(sketch, "E334.0", {"position": v(762, -25.4) * mm});
            skPoint(sketch, "E335.0", {"position": v(-762, -25.4) * mm});
            skLineSegment(sketch, "E336", {"start": v(-762, -25.4) * mm, "end": v(762, -25.4) * mm});
            skLineSegment(sketch, "E337", {"start": v(-762, -25.4) * mm, "end": v(-762, 0) * mm});
            skLineSegment(sketch, "E338", {"start": v(-762, 0) * mm, "end": v(762, 0) * mm});
            skLineSegment(sketch, "E339", {"start": v(762, 0) * mm, "end": v(762, -25.4) * mm});
            skSolve(sketch);
        }
        {
            var Q0;
            Q0=makeQuery(id+"F90.imprint","IMPRINT",FACE,{"disambiguationData":[TD([[makeQuery(id+"F90.imprint","IMPRINT",EDGE,{"derivedFrom":sQuery(id+"F90.wireOp",EDGE,"E336")}),1.0]])]});
            extrude(context, id + "F91", {"entities" : qUnion([Q0]), "endBound" : BoundingType.SYMMETRIC, "depth" : 38.1 * mm});
        }
        {
            var Q0;
            Q0=makeQuery(id+"F91.opExtrude","SWEPT_FACE",FACE,{"disambiguationData":[OSD([sQuery(id+"F90.wireOp",EDGE,"E337")])]});
            var sketch = newSketch(context, id + "F92", { "sketchPlane" : qUnion([Q0])});
            skLineSegment(sketch, "E340.bottom", {"start": v(-12.7, -4.45) * mm, "end": v(12.7, -4.45) * mm});
            skLineSegment(sketch, "E340.top", {"start": v(-12.7, -20.95) * mm, "end": v(12.7, -20.95) * mm});
            skLineSegment(sketch, "E340.left", {"start": v(-12.7, -4.45) * mm, "end": v(-12.7, -20.95) * mm});
            skLineSegment(sketch, "E340.right", {"start": v(12.7, -4.45) * mm, "end": v(12.7, -20.95) * mm});
            skSolve(sketch);
        }
        {
            var Q0;
            Q0=makeQuery(id+"F92.imprint","IMPRINT",FACE,{"disambiguationData":[TD([[makeQuery(id+"F92.imprint","IMPRINT",EDGE,{"derivedFrom":sQuery(id+"F92.wireOp",EDGE,"E340.bottom")}),-1.0]])]});
            extrude(context, id + "F93", {"entities" : qUnion([Q0]), "operationType" : NewBodyOperationType.REMOVE, "endBound" : BoundingType.THROUGH_ALL, "oppositeDirection" : true, "depth" : 25.4 * mm});
        }
    });
